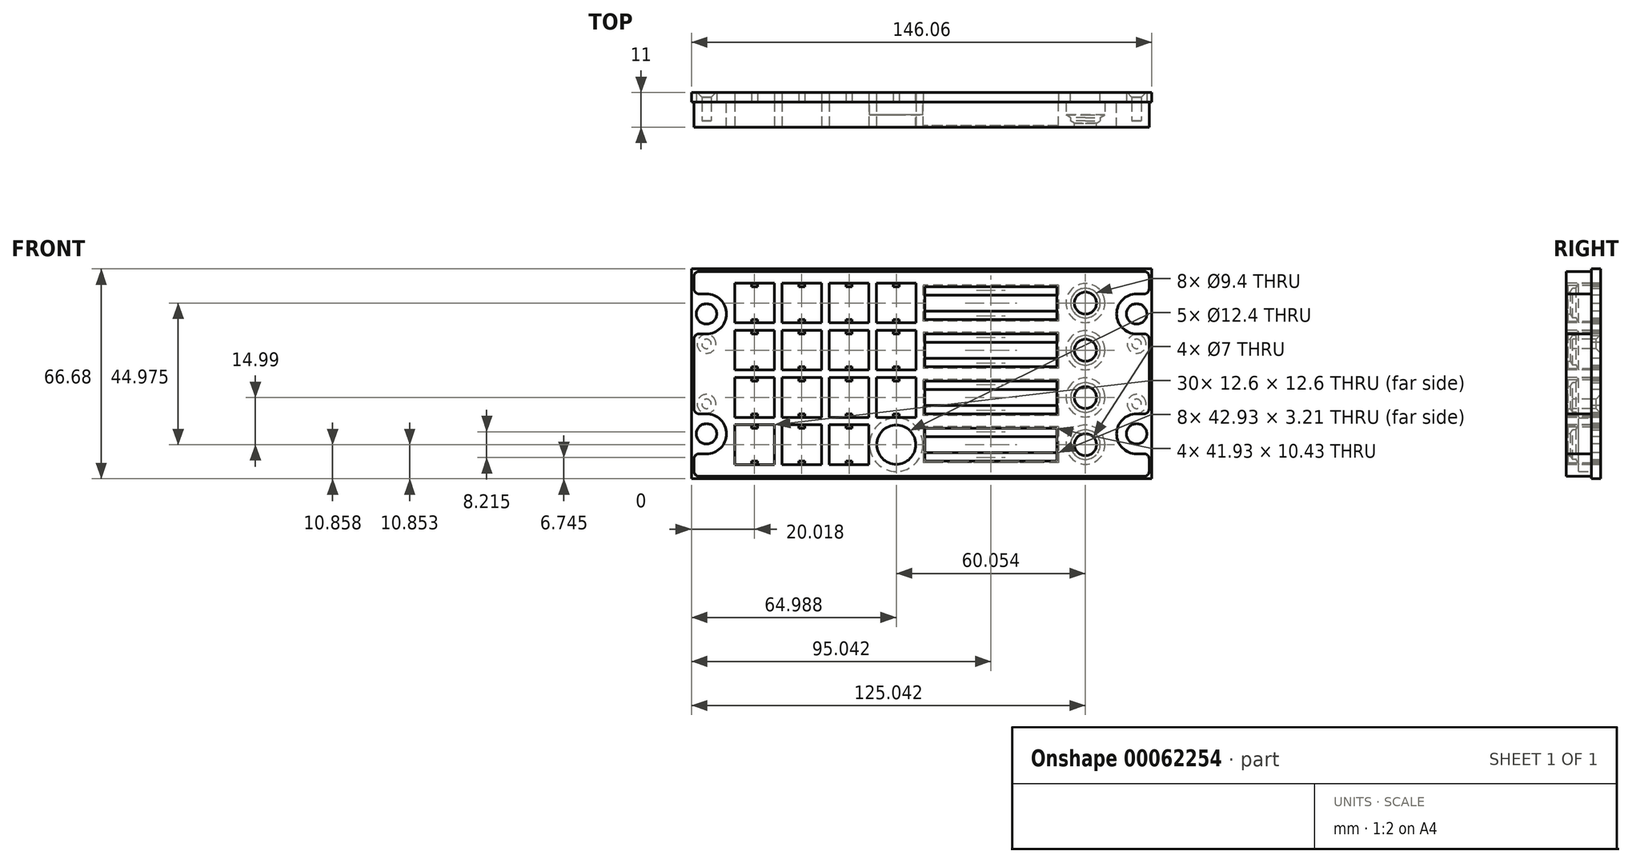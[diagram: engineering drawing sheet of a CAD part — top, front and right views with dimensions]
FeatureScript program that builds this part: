
annotation { "Feature Type Name" : "Feature", "Feature Type Description" : "" }
export const myFeature = defineFeature(function(context is Context, id is Id, definition is map)
    precondition{}
    {
        {
            var Q0;
            Q0=qCreatedBy(makeId("Front.planeOp"),FACE);
            var sketch = newSketch(context, id + "F0", { "sketchPlane" : qUnion([Q0])});
            skCircle(sketch, "E0", {"center": v(68.26, 19.05) * mm, "radius": 3.24 * mm});
            skCircle(sketch, "E1", {"center": v(68.26, -19.05) * mm, "radius": 3.24 * mm});
            skLineSegment(sketch, "E2", {"start": v(73.03, -33.34) * mm, "end": v(73.03, 33.34) * mm});
            skLineSegment(sketch, "E3", {"start": v(-73.03, 33.34) * mm, "end": v(73.03, 33.34) * mm});
            skLineSegment(sketch, "E4", {"start": v(-73.03, -33.34) * mm, "end": v(-73.03, 33.34) * mm});
            skLineSegment(sketch, "E5", {"start": v(73.03, -33.34) * mm, "end": v(-73.03, -33.34) * mm});
            skCircle(sketch, "E6", {"center": v(-68.26, -19.05) * mm, "radius": 3.24 * mm});
            skCircle(sketch, "E7", {"center": v(-68.26, 19.05) * mm, "radius": 3.24 * mm});
            skSolve(sketch);
        }
        {
            var Q0;
            Q0=makeQuery(id+"F0.imprint","IMPRINT",FACE,{"disambiguationData":[TD([[makeQuery(id+"F0.imprint","IMPRINT",EDGE,{"derivedFrom":sQuery(id+"F0.wireOp",EDGE,"E3")}),-1.0]])]});
            var Q1;
            Q1=makeQuery(id+"F0.imprint","IMPRINT",FACE,{"disambiguationData":[TD([[makeQuery(id+"F0.imprint","IMPRINT",EDGE,{"derivedFrom":sQuery(id+"F0.wireOp",EDGE,"PkqqOQiF-yNax-qwMA-xXQ1-8JkGYJM5UorW")}),-1.0]])]});
            var Q2;
            Q2=makeQuery(id+"F0.imprint","IMPRINT",FACE,{"disambiguationData":[TD([[makeQuery(id+"F0.imprint","IMPRINT",EDGE,{"derivedFrom":sQuery(id+"F0.wireOp",EDGE,"mQLwxlvx-ERE5-Mz6w-w5xm-fzkBPykc801v")}),-1.0]])]});
            var Q3;
            {var subQ0=sQuery(id+"F0.wireOp",EDGE,"rYfaxixD-Fold-LEk9-B7Sj-y0uFZKrMDMnr");Q3=makeQuery(id+"F0.imprint","IMPRINT",FACE,{"disambiguationData":[TD([[makeQuery(id+"F0.imprint","IMPRINT",EDGE,{"derivedFrom":subQ0}),1.0]])]});}
            var Q4;
            {var subQ0=sQuery(id+"F0.wireOp",EDGE,"rYfaxixD-Fold-LEk9-B7Sj-y0uFZKrMDMnr");Q4=makeQuery(id+"F0.imprint","IMPRINT",FACE,{"disambiguationData":[TD([[makeQuery(id+"F0.imprint","IMPRINT",EDGE,{"derivedFrom":subQ0}),-1.0]])]});}
            var Q5;
            {var subQ0=sQuery(id+"F0.wireOp",EDGE,"O9xndx6B-X1w8-GipV-mM2N-SATMcNrLLSkd");Q5=makeQuery(id+"F0.imprint","IMPRINT",FACE,{"disambiguationData":[TD([[makeQuery(id+"F0.imprint","IMPRINT",EDGE,{"derivedFrom":subQ0}),1.0]])]});}
            var Q6;
            {var subQ0=sQuery(id+"F0.wireOp",EDGE,"O9xndx6B-X1w8-GipV-mM2N-SATMcNrLLSkd");Q6=makeQuery(id+"F0.imprint","IMPRINT",FACE,{"disambiguationData":[TD([[makeQuery(id+"F0.imprint","IMPRINT",EDGE,{"derivedFrom":subQ0}),-1.0]])]});}
            extrude(context, id + "F1", {"entities" : qUnion([Q0, Q1, Q2, Q3, Q4, Q5, Q6]), "oppositeDirection" : true, "depth" : 3 * mm});
        }
        {
            var Q0;
            Q0=makeQuery(id+"F0.imprint","IMPRINT",FACE,{"disambiguationData":[TD([[makeQuery(id+"F0.imprint","IMPRINT",EDGE,{"derivedFrom":sQuery(id+"F0.wireOp",EDGE,"E3")}),-1.0]])]});
            var sketch = newSketch(context, id + "F2", { "sketchPlane" : qUnion([Q0])});
            skLineSegment(sketch, "E8", {"start": v(-68.26, 12.7) * mm, "end": v(-72.23, 12.7) * mm});
            skArc(sketch, "E9", {"start": v(-68.26, -25.4) * mm, "mid": v(-61.91, -19.05) * mm, "end": v(-68.26, -12.7) * mm});
            skArc(sketch, "E10", {"start": v(68.26, -12.7) * mm, "mid": v(61.91, -19.05) * mm, "end": v(68.26, -25.4) * mm});
            skLineSegment(sketch, "E11", {"start": v(72.22, -32.54) * mm, "end": v(72.22, -25.4) * mm});
            skLineSegment(sketch, "E12", {"start": v(-72.23, -32.54) * mm, "end": v(-72.23, -25.4) * mm});
            skLineSegment(sketch, "E13", {"start": v(72.22, -32.54) * mm, "end": v(-72.23, -32.54) * mm});
            skArc(sketch, "E14", {"start": v(68.26, 25.4) * mm, "mid": v(61.91, 19.05) * mm, "end": v(68.26, 12.7) * mm});
            skLineSegment(sketch, "E15", {"start": v(-72.23, 32.54) * mm, "end": v(72.23, 32.54) * mm});
            skLineSegment(sketch, "E16", {"start": v(68.26, 12.7) * mm, "end": v(72.22, 12.7) * mm});
            skLineSegment(sketch, "E17", {"start": v(68.26, 25.4) * mm, "end": v(72.22, 25.4) * mm});
            skLineSegment(sketch, "E18", {"start": v(72.22, -12.7) * mm, "end": v(72.22, 12.7) * mm});
            skLineSegment(sketch, "E19", {"start": v(68.26, -12.7) * mm, "end": v(72.22, -12.7) * mm});
            skLineSegment(sketch, "E20", {"start": v(-68.26, -12.7) * mm, "end": v(-72.23, -12.7) * mm});
            skLineSegment(sketch, "E21", {"start": v(68.26, -25.4) * mm, "end": v(72.22, -25.4) * mm});
            skLineSegment(sketch, "E22", {"start": v(-72.23, -12.7) * mm, "end": v(-72.23, 12.7) * mm});
            skArc(sketch, "E23", {"start": v(-68.26, 12.7) * mm, "mid": v(-61.91, 19.05) * mm, "end": v(-68.26, 25.4) * mm});
            skLineSegment(sketch, "E24", {"start": v(-72.23, 25.4) * mm, "end": v(-72.23, 32.54) * mm});
            skLineSegment(sketch, "E25", {"start": v(-68.26, 25.4) * mm, "end": v(-72.23, 25.4) * mm});
            skLineSegment(sketch, "E26", {"start": v(-68.26, -25.4) * mm, "end": v(-72.23, -25.4) * mm});
            skLineSegment(sketch, "E27", {"start": v(72.22, 25.4) * mm, "end": v(72.22, 32.54) * mm});
            skCircle(sketch, "E28", {"center": v(68.26, 19.05) * mm, "radius": 3.24 * mm});
            skCircle(sketch, "E29", {"center": v(68.26, -19.05) * mm, "radius": 3.24 * mm});
            skLineSegment(sketch, "E30", {"start": v(73.03, -33.34) * mm, "end": v(73.03, 33.34) * mm});
            skLineSegment(sketch, "E31", {"start": v(-73.03, 33.34) * mm, "end": v(73.03, 33.34) * mm});
            skLineSegment(sketch, "E32", {"start": v(-73.03, -33.34) * mm, "end": v(-73.03, 33.34) * mm});
            skLineSegment(sketch, "E33", {"start": v(73.03, -33.34) * mm, "end": v(-73.03, -33.34) * mm});
            skCircle(sketch, "E34", {"center": v(-68.26, -19.05) * mm, "radius": 3.24 * mm});
            skCircle(sketch, "E35", {"center": v(-68.26, 19.05) * mm, "radius": 3.24 * mm});
            skPoint(sketch, "E36.middle", {"position": v(-53.01, 22.49) * mm});
            skPoint(sketch, "E37.middle", {"position": v(-53.01, 7.5) * mm});
            skLineSegment(sketch, "E38", {"start": v(-53.01, 22.49) * mm, "end": v(-53.01, 23.47) * mm});
            skLineSegment(sketch, "E39", {"start": v(-53.01, 22.49) * mm, "end": v(-52.23, 22.49) * mm});
            skLineSegment(sketch, "E40.MirrorCS", {"start": v(-50.56, 16.89) * mm, "end": v(-50.56, 16.29) * mm});
            skLineSegment(sketch, "E41", {"start": v(-51.55, 16.29) * mm, "end": v(-51.55, 13.7) * mm});
            skLineSegment(sketch, "E42", {"start": v(-45.52, 24.36) * mm, "end": v(-45.52, 21.49) * mm});
            skLineSegment(sketch, "E43", {"start": v(-51.55, 15) * mm, "end": v(-52.76, 15) * mm});
            skPoint(sketch, "E44", {"position": v(-45.52, 22.92) * mm});
            skPoint(sketch, "E45", {"position": v(-52.76, 15) * mm});
            skPoint(sketch, "E46", {"position": v(-30.53, 22.49) * mm});
            skLineSegment(sketch, "E47.bottom", {"start": v(-46.76, 13.75) * mm, "end": v(-59.26, 13.75) * mm});
            skLineSegment(sketch, "E47.top", {"start": v(-46.76, 1.25) * mm, "end": v(-59.26, 1.25) * mm});
            skLineSegment(sketch, "E47.left", {"start": v(-46.76, 13.75) * mm, "end": v(-46.76, 1.25) * mm});
            skLineSegment(sketch, "E47.right", {"start": v(-59.26, 13.75) * mm, "end": v(-59.26, 1.25) * mm});
            skLineSegment(sketch, "E48.MirrorCS", {"start": v(-46.76, 16.24) * mm, "end": v(-59.26, 16.24) * mm});
            skLineSegment(sketch, "E49.MirrorCS", {"start": v(-59.26, 16.24) * mm, "end": v(-59.26, 28.74) * mm});
            skLineSegment(sketch, "E50.MirrorCS", {"start": v(-46.76, 16.24) * mm, "end": v(-46.76, 28.74) * mm});
            skLineSegment(sketch, "E51.MirrorCS", {"start": v(-46.76, 28.74) * mm, "end": v(-59.26, 28.74) * mm});
            skLineSegment(sketch, "E52.MirrorCS", {"start": v(-44.27, 16.24) * mm, "end": v(-44.27, 28.74) * mm});
            skLineSegment(sketch, "E53.MirrorCS", {"start": v(-44.27, 28.74) * mm, "end": v(-31.77, 28.74) * mm});
            skLineSegment(sketch, "E54.MirrorCS", {"start": v(-31.77, 16.24) * mm, "end": v(-31.77, 28.74) * mm});
            skLineSegment(sketch, "E55.MirrorCS", {"start": v(-44.27, 16.24) * mm, "end": v(-31.77, 16.24) * mm});
            skLineSegment(sketch, "E56", {"start": v(-30.53, 22.49) * mm, "end": v(-30.53, 24.6) * mm});
            skLineSegment(sketch, "E57.MirrorCS", {"start": v(-29.28, 16.24) * mm, "end": v(-29.28, 28.74) * mm});
            skLineSegment(sketch, "E58.MirrorCS", {"start": v(-16.78, 28.74) * mm, "end": v(-29.28, 28.74) * mm});
            skLineSegment(sketch, "E59.MirrorCS", {"start": v(-14.3, 28.74) * mm, "end": v(-1.8, 28.74) * mm});
            skLineSegment(sketch, "E60.MirrorCS", {"start": v(-1.8, 16.24) * mm, "end": v(-1.8, 28.74) * mm});
            skLineSegment(sketch, "E61.MirrorCS", {"start": v(-14.3, 16.24) * mm, "end": v(-1.8, 16.24) * mm});
            skLineSegment(sketch, "E62.MirrorCS", {"start": v(-14.3, 16.24) * mm, "end": v(-14.3, 28.74) * mm});
            skLineSegment(sketch, "E63.MirrorCS", {"start": v(-16.78, 16.24) * mm, "end": v(-16.78, 28.74) * mm});
            skLineSegment(sketch, "E64.MirrorCS", {"start": v(-16.78, 16.24) * mm, "end": v(-29.28, 16.24) * mm});
            skLineSegment(sketch, "E65.MirrorCS", {"start": v(-29.28, 13.75) * mm, "end": v(-29.28, 1.25) * mm});
            skLineSegment(sketch, "E66.MirrorCS", {"start": v(-30.53, 7.5) * mm, "end": v(-30.53, 5.4) * mm});
            skLineSegment(sketch, "E67.MirrorCS", {"start": v(-44.27, 13.75) * mm, "end": v(-31.77, 13.75) * mm});
            skLineSegment(sketch, "E68.MirrorCS", {"start": v(-16.78, 1.25) * mm, "end": v(-29.28, 1.25) * mm});
            skPoint(sketch, "E69.MirrorP", {"position": v(-30.53, 7.5) * mm});
            skLineSegment(sketch, "E70.MirrorCS", {"start": v(-16.78, 13.75) * mm, "end": v(-16.78, 1.25) * mm});
            skLineSegment(sketch, "E71.MirrorCS", {"start": v(-14.3, 1.25) * mm, "end": v(-1.8, 1.25) * mm});
            skLineSegment(sketch, "E72.MirrorCS", {"start": v(-44.27, 13.75) * mm, "end": v(-44.27, 1.25) * mm});
            skLineSegment(sketch, "E73.MirrorCS", {"start": v(-14.3, 13.75) * mm, "end": v(-1.8, 13.75) * mm});
            skLineSegment(sketch, "E74.MirrorCS", {"start": v(-14.3, 13.75) * mm, "end": v(-14.3, 1.25) * mm});
            skLineSegment(sketch, "E75.MirrorCS", {"start": v(-44.27, 1.25) * mm, "end": v(-31.77, 1.25) * mm});
            skLineSegment(sketch, "E76.MirrorCS", {"start": v(-31.77, 13.75) * mm, "end": v(-31.77, 1.25) * mm});
            skLineSegment(sketch, "E77.MirrorCS", {"start": v(-1.8, 13.75) * mm, "end": v(-1.8, 1.25) * mm});
            skPoint(sketch, "E78.MirrorP", {"position": v(-45.52, 7.06) * mm});
            skLineSegment(sketch, "E79.MirrorCS", {"start": v(-16.78, 13.75) * mm, "end": v(-29.28, 13.75) * mm});
            skLineSegment(sketch, "E80.MirrorCS", {"start": v(-53.01, -22.49) * mm, "end": v(-52.23, -22.49) * mm});
            skLineSegment(sketch, "E81.MirrorCS", {"start": v(-53.01, -22.49) * mm, "end": v(-53.01, -23.47) * mm});
            skPoint(sketch, "E82.MirrorP", {"position": v(-53.01, -7.5) * mm});
            skLineSegment(sketch, "E83.MirrorCS", {"start": v(-29.28, -13.75) * mm, "end": v(-29.28, -1.25) * mm});
            skLineSegment(sketch, "E84.MirrorCS", {"start": v(-30.53, -7.5) * mm, "end": v(-30.53, -5.4) * mm});
            skLineSegment(sketch, "E85.MirrorCS", {"start": v(-51.55, -15) * mm, "end": v(-52.76, -15) * mm});
            skLineSegment(sketch, "E86.MirrorCS", {"start": v(-51.55, -16.29) * mm, "end": v(-51.55, -13.7) * mm});
            skLineSegment(sketch, "E87.MirrorCS", {"start": v(-29.28, -16.24) * mm, "end": v(-29.28, -28.74) * mm});
            skLineSegment(sketch, "E88.MirrorCS", {"start": v(-50.56, -16.89) * mm, "end": v(-50.56, -16.29) * mm});
            skLineSegment(sketch, "E89.MirrorCS", {"start": v(-30.53, -22.49) * mm, "end": v(-30.53, -24.6) * mm});
            skLineSegment(sketch, "E90.MirrorCS", {"start": v(-45.52, -24.36) * mm, "end": v(-45.52, -21.49) * mm});
            skPoint(sketch, "E91.MirrorP", {"position": v(-53.01, -22.49) * mm});
            skLineSegment(sketch, "E92.MirrorCS", {"start": v(-46.76, -1.25) * mm, "end": v(-59.26, -1.25) * mm});
            skPoint(sketch, "E93.MirrorP", {"position": v(-52.76, -15) * mm});
            skPoint(sketch, "E94.MirrorP", {"position": v(-45.52, -7.06) * mm});
            skPoint(sketch, "E95.MirrorP", {"position": v(-45.52, -22.92) * mm});
            skLineSegment(sketch, "E96.MirrorCS", {"start": v(-31.77, -16.24) * mm, "end": v(-31.77, -28.74) * mm});
            skLineSegment(sketch, "E97.MirrorCS", {"start": v(-44.27, -28.74) * mm, "end": v(-31.77, -28.74) * mm});
            skLineSegment(sketch, "E98.MirrorCS", {"start": v(-44.27, -1.25) * mm, "end": v(-31.77, -1.25) * mm});
            skLineSegment(sketch, "E99.MirrorCS", {"start": v(-16.78, -1.25) * mm, "end": v(-29.28, -1.25) * mm});
            skLineSegment(sketch, "E100.MirrorCS", {"start": v(-16.78, -13.75) * mm, "end": v(-16.78, -1.25) * mm});
            skLineSegment(sketch, "E101.MirrorCS", {"start": v(-31.77, -13.75) * mm, "end": v(-31.77, -1.25) * mm});
            skLineSegment(sketch, "E102.MirrorCS", {"start": v(-14.3, -13.75) * mm, "end": v(-1.8, -13.75) * mm});
            skLineSegment(sketch, "E103.MirrorCS", {"start": v(-59.26, -13.75) * mm, "end": v(-59.26, -1.25) * mm});
            skLineSegment(sketch, "E104.MirrorCS", {"start": v(-14.3, -13.75) * mm, "end": v(-14.3, -1.25) * mm});
            skLineSegment(sketch, "E105.MirrorCS", {"start": v(-44.27, -16.24) * mm, "end": v(-44.27, -28.74) * mm});
            skLineSegment(sketch, "E106.MirrorCS", {"start": v(-16.78, -28.74) * mm, "end": v(-29.28, -28.74) * mm});
            skLineSegment(sketch, "E107.MirrorCS", {"start": v(-16.78, -16.24) * mm, "end": v(-29.28, -16.24) * mm});
            skLineSegment(sketch, "E108.MirrorCS", {"start": v(-1.8, -13.75) * mm, "end": v(-1.8, -1.25) * mm});
            skLineSegment(sketch, "E109.MirrorCS", {"start": v(-44.27, -16.24) * mm, "end": v(-31.77, -16.24) * mm});
            skLineSegment(sketch, "E110.MirrorCS", {"start": v(-14.3, -1.25) * mm, "end": v(-1.8, -1.25) * mm});
            skLineSegment(sketch, "E111.MirrorCS", {"start": v(-46.76, -16.24) * mm, "end": v(-59.26, -16.24) * mm});
            skLineSegment(sketch, "E112.MirrorCS", {"start": v(-46.76, -16.24) * mm, "end": v(-46.76, -28.74) * mm});
            skLineSegment(sketch, "E113.MirrorCS", {"start": v(-59.26, -16.24) * mm, "end": v(-59.26, -28.74) * mm});
            skLineSegment(sketch, "E114.MirrorCS", {"start": v(-16.78, -16.24) * mm, "end": v(-16.78, -28.74) * mm});
            skLineSegment(sketch, "E115.MirrorCS", {"start": v(-46.76, -13.75) * mm, "end": v(-46.76, -1.25) * mm});
            skLineSegment(sketch, "E116.MirrorCS", {"start": v(-44.27, -13.75) * mm, "end": v(-31.77, -13.75) * mm});
            skLineSegment(sketch, "E117.MirrorCS", {"start": v(-16.78, -13.75) * mm, "end": v(-29.28, -13.75) * mm});
            skLineSegment(sketch, "E118.MirrorCS", {"start": v(-46.76, -28.74) * mm, "end": v(-59.26, -28.74) * mm});
            skPoint(sketch, "E119.MirrorP", {"position": v(-30.53, -22.49) * mm});
            skPoint(sketch, "E120.MirrorP", {"position": v(-30.53, -7.5) * mm});
            skLineSegment(sketch, "E121.MirrorCS", {"start": v(-44.27, -13.75) * mm, "end": v(-44.27, -1.25) * mm});
            skLineSegment(sketch, "E122.MirrorCS", {"start": v(-46.76, -13.75) * mm, "end": v(-59.26, -13.75) * mm});
            skLineSegment(sketch, "E123.bottom", {"start": v(-59.26, 28.74) * mm, "end": v(-58.01, 28.74) * mm});
            skLineSegment(sketch, "E123.top", {"start": v(-59.26, 27.49) * mm, "end": v(-58.01, 27.49) * mm});
            skLineSegment(sketch, "E123.left", {"start": v(-59.26, 28.74) * mm, "end": v(-59.26, 27.49) * mm});
            skLineSegment(sketch, "E123.right", {"start": v(-58.01, 28.74) * mm, "end": v(-58.01, 27.49) * mm});
            skLineSegment(sketch, "E124.MirrorCS", {"start": v(-48.01, 28.74) * mm, "end": v(-48.01, 27.49) * mm});
            skLineSegment(sketch, "E125.MirrorCS", {"start": v(-46.76, 27.49) * mm, "end": v(-48.01, 27.49) * mm});
            skLineSegment(sketch, "E126.MirrorCS", {"start": v(-43.02, 28.74) * mm, "end": v(-43.02, 27.49) * mm});
            skLineSegment(sketch, "E127.MirrorCS", {"start": v(-44.27, 27.49) * mm, "end": v(-43.02, 27.49) * mm});
            skLineSegment(sketch, "E128.MirrorCS", {"start": v(-33.02, 28.74) * mm, "end": v(-33.02, 27.49) * mm});
            skLineSegment(sketch, "E129.MirrorCS", {"start": v(-31.77, 27.49) * mm, "end": v(-33.02, 27.49) * mm});
            skLineSegment(sketch, "E130.MirrorCS", {"start": v(-28.03, 28.74) * mm, "end": v(-28.03, 27.49) * mm});
            skLineSegment(sketch, "E131.MirrorCS", {"start": v(-29.28, 27.49) * mm, "end": v(-28.03, 27.49) * mm});
            skLineSegment(sketch, "E132.MirrorCS", {"start": v(-18.03, 28.74) * mm, "end": v(-18.03, 27.49) * mm});
            skLineSegment(sketch, "E133.MirrorCS", {"start": v(-16.78, 27.49) * mm, "end": v(-18.03, 27.49) * mm});
            skLineSegment(sketch, "E134.MirrorCS", {"start": v(-13.04, 28.74) * mm, "end": v(-13.04, 27.49) * mm});
            skLineSegment(sketch, "E135.MirrorCS", {"start": v(-14.3, 27.49) * mm, "end": v(-13.04, 27.49) * mm});
            skLineSegment(sketch, "E136.MirrorCS", {"start": v(-3.04, 28.74) * mm, "end": v(-3.04, 27.49) * mm});
            skLineSegment(sketch, "E137.MirrorCS", {"start": v(-1.8, 27.49) * mm, "end": v(-3.04, 27.49) * mm});
            skLineSegment(sketch, "E138.bottom", {"start": v(-59.26, 13.75) * mm, "end": v(-58.01, 13.75) * mm});
            skLineSegment(sketch, "E138.top", {"start": v(-59.26, 12.5) * mm, "end": v(-58.01, 12.5) * mm});
            skLineSegment(sketch, "E138.left", {"start": v(-59.26, 13.75) * mm, "end": v(-59.26, 12.5) * mm});
            skLineSegment(sketch, "E138.right", {"start": v(-58.01, 13.75) * mm, "end": v(-58.01, 12.5) * mm});
            skLineSegment(sketch, "E139.MirrorCS", {"start": v(-48.01, 13.75) * mm, "end": v(-48.01, 12.5) * mm});
            skLineSegment(sketch, "E140.MirrorCS", {"start": v(-46.76, 12.5) * mm, "end": v(-48.01, 12.5) * mm});
            skLineSegment(sketch, "E141.MirrorCS", {"start": v(-33.02, 13.75) * mm, "end": v(-33.02, 12.5) * mm});
            skLineSegment(sketch, "E142.MirrorCS", {"start": v(-31.77, 12.5) * mm, "end": v(-33.02, 12.5) * mm});
            skLineSegment(sketch, "E143.MirrorCS", {"start": v(-43.02, 13.75) * mm, "end": v(-43.02, 12.5) * mm});
            skLineSegment(sketch, "E144.MirrorCS", {"start": v(-44.27, 12.5) * mm, "end": v(-43.02, 12.5) * mm});
            skLineSegment(sketch, "E145.MirrorCS", {"start": v(-28.03, 13.75) * mm, "end": v(-28.03, 12.5) * mm});
            skLineSegment(sketch, "E146.MirrorCS", {"start": v(-29.28, 12.5) * mm, "end": v(-28.03, 12.5) * mm});
            skLineSegment(sketch, "E147.MirrorCS", {"start": v(-18.03, 13.75) * mm, "end": v(-18.03, 12.5) * mm});
            skLineSegment(sketch, "E148.MirrorCS", {"start": v(-16.78, 12.5) * mm, "end": v(-18.03, 12.5) * mm});
            skLineSegment(sketch, "E149.MirrorCS", {"start": v(-3.04, 13.75) * mm, "end": v(-3.04, 12.5) * mm});
            skLineSegment(sketch, "E150.MirrorCS", {"start": v(-1.8, 12.5) * mm, "end": v(-3.04, 12.5) * mm});
            skLineSegment(sketch, "E151.MirrorCS", {"start": v(-13.04, 13.75) * mm, "end": v(-13.04, 12.5) * mm});
            skLineSegment(sketch, "E152.MirrorCS", {"start": v(-14.3, 12.5) * mm, "end": v(-13.04, 12.5) * mm});
            skLineSegment(sketch, "E153.bottom", {"start": v(-59.26, -1.25) * mm, "end": v(-58.01, -1.25) * mm});
            skLineSegment(sketch, "E153.top", {"start": v(-59.26, -2.5) * mm, "end": v(-58.01, -2.5) * mm});
            skLineSegment(sketch, "E153.left", {"start": v(-59.26, -1.25) * mm, "end": v(-59.26, -2.5) * mm});
            skLineSegment(sketch, "E153.right", {"start": v(-58.01, -1.25) * mm, "end": v(-58.01, -2.5) * mm});
            skLineSegment(sketch, "E154.MirrorCS", {"start": v(-48.01, -1.25) * mm, "end": v(-48.01, -2.5) * mm});
            skLineSegment(sketch, "E155.MirrorCS", {"start": v(-46.76, -2.5) * mm, "end": v(-48.01, -2.5) * mm});
            skLineSegment(sketch, "E156.MirrorCS", {"start": v(-43.02, -1.25) * mm, "end": v(-43.02, -2.5) * mm});
            skLineSegment(sketch, "E157.MirrorCS", {"start": v(-44.27, -2.5) * mm, "end": v(-43.02, -2.5) * mm});
            skLineSegment(sketch, "E158.MirrorCS", {"start": v(-33.02, -1.25) * mm, "end": v(-33.02, -2.5) * mm});
            skLineSegment(sketch, "E159.MirrorCS", {"start": v(-31.77, -2.5) * mm, "end": v(-33.02, -2.5) * mm});
            skLineSegment(sketch, "E160.MirrorCS", {"start": v(-60.5, -7.5) * mm, "end": v(-60.5, -5.4) * mm});
            skLineSegment(sketch, "E161.MirrorCS", {"start": v(-1.8, -2.5) * mm, "end": v(-3.04, -2.5) * mm});
            skLineSegment(sketch, "E162.MirrorCS", {"start": v(-3.04, -1.25) * mm, "end": v(-3.04, -2.5) * mm});
            skLineSegment(sketch, "E163.MirrorCS", {"start": v(-13.04, -1.25) * mm, "end": v(-13.04, -2.5) * mm});
            skLineSegment(sketch, "E164.MirrorCS", {"start": v(-14.3, -2.5) * mm, "end": v(-13.04, -2.5) * mm});
            skLineSegment(sketch, "E165.MirrorCS", {"start": v(-16.78, -2.5) * mm, "end": v(-18.03, -2.5) * mm});
            skLineSegment(sketch, "E166.MirrorCS", {"start": v(-18.03, -1.25) * mm, "end": v(-18.03, -2.5) * mm});
            skLineSegment(sketch, "E167.MirrorCS", {"start": v(-28.03, -1.25) * mm, "end": v(-28.03, -2.5) * mm});
            skLineSegment(sketch, "E168.MirrorCS", {"start": v(-29.28, -2.5) * mm, "end": v(-28.03, -2.5) * mm});
            skLineSegment(sketch, "E169.bottom", {"start": v(-59.26, -16.24) * mm, "end": v(-58.01, -16.24) * mm});
            skLineSegment(sketch, "E169.top", {"start": v(-59.26, -17.49) * mm, "end": v(-58.01, -17.49) * mm});
            skLineSegment(sketch, "E169.left", {"start": v(-59.26, -16.24) * mm, "end": v(-59.26, -17.49) * mm});
            skLineSegment(sketch, "E169.right", {"start": v(-58.01, -16.24) * mm, "end": v(-58.01, -17.49) * mm});
            skLineSegment(sketch, "E170.MirrorCS", {"start": v(-48.01, -16.24) * mm, "end": v(-48.01, -17.49) * mm});
            skLineSegment(sketch, "E171.MirrorCS", {"start": v(-46.76, -17.49) * mm, "end": v(-48.01, -17.49) * mm});
            skLineSegment(sketch, "E172.MirrorCS", {"start": v(-43.02, -16.24) * mm, "end": v(-43.02, -17.49) * mm});
            skLineSegment(sketch, "E173.MirrorCS", {"start": v(-44.27, -17.49) * mm, "end": v(-43.02, -17.49) * mm});
            skLineSegment(sketch, "E174.MirrorCS", {"start": v(-33.02, -16.24) * mm, "end": v(-33.02, -17.49) * mm});
            skLineSegment(sketch, "E175.MirrorCS", {"start": v(-31.77, -17.49) * mm, "end": v(-33.02, -17.49) * mm});
            skLineSegment(sketch, "E176.MirrorCS", {"start": v(-28.03, -16.24) * mm, "end": v(-28.03, -17.49) * mm});
            skLineSegment(sketch, "E177.MirrorCS", {"start": v(-29.28, -17.49) * mm, "end": v(-28.03, -17.49) * mm});
            skLineSegment(sketch, "E178.MirrorCS", {"start": v(-18.03, -16.24) * mm, "end": v(-18.03, -17.49) * mm});
            skLineSegment(sketch, "E179.MirrorCS", {"start": v(-16.78, -17.49) * mm, "end": v(-18.03, -17.49) * mm});
            skSolve(sketch);
        }
        {
            var Q0;
            Q0=makeQuery(id+"F2.imprint","IMPRINT",FACE,{"disambiguationData":[TD([[makeQuery(id+"F2.imprint","IMPRINT",EDGE,{"derivedFrom":sQuery(id+"F2.wireOp",EDGE,"E25")}),-1.0]])]});
            var Q1;
            Q1=makeQuery(id+"F2.imprint","IMPRINT",FACE,{"disambiguationData":[TD([[makeQuery(id+"F2.imprint","IMPRINT",EDGE,{"derivedFrom":sQuery(id+"F2.wireOp",EDGE,"E19")}),1.0]])]});
            var Q2;
            Q2=makeQuery(id+"F2.imprint","IMPRINT",FACE,{"disambiguationData":[TD([[makeQuery(id+"F2.imprint","IMPRINT",EDGE,{"derivedFrom":sQuery(id+"F2.wireOp",EDGE,"qFL4g8N9-Z4pU-GTXp-8CAc-8JK48FUQn30E")}),-1.0]])]});
            var Q3;
            {var subQ0=sQuery(id+"F2.wireOp",EDGE,"8300f3b8-7403-4ca9-be41-47c3c9048a200.MirrorCS");var subQ1=sQuery(id+"F2.wireOp",EDGE,"vQyVyV5x-p2yk-mqKs-SuCr-8gVJOWqc7IX1");var subQ2=makeQuery(id+"F2.imprint","INTERSECT",VERTEX,{"disambiguationData":[OD(0.0)],"derivedFrom":[subQ1,subQ0]});Q3=makeQuery(id+"F2.imprint","IMPRINT",FACE,{"disambiguationData":[TD([[makeQuery(id+"F2.imprint","IMPRINT",EDGE,{"disambiguationData":[TD([[subQ2,-1.0]])],"derivedFrom":subQ1}),-1.0]])]});}
            var Q4;
            {var subQ0=sQuery(id+"F2.wireOp",EDGE,"2a6b824b-4dab-4004-b1fb-ce6e91d1ccc60.MirrorCS");var subQ1=sQuery(id+"F2.wireOp",EDGE,"vQyVyV5x-p2yk-mqKs-SuCr-8gVJOWqc7IX1");var subQ2=makeQuery(id+"F2.imprint","INTERSECT",VERTEX,{"disambiguationData":[OD(1.0)],"derivedFrom":[subQ1,subQ0]});Q4=makeQuery(id+"F2.imprint","IMPRINT",FACE,{"disambiguationData":[TD([[makeQuery(id+"F2.imprint","IMPRINT",EDGE,{"disambiguationData":[TD([[subQ2,-1.0]])],"derivedFrom":subQ1}),-1.0]])]});}
            var Q5;
            {var subQ1=sQuery(id+"F2.wireOp",EDGE,"670ac697-91f2-46ae-bd51-22720ef3b4b70.MirrorCS");var subQ7=sQuery(id+"F2.wireOp",EDGE,"vQyVyV5x-p2yk-mqKs-SuCr-8gVJOWqc7IX1");var subQ9=makeQuery(id+"F2.imprint","INTERSECT",VERTEX,{"disambiguationData":[OD(0.0)],"derivedFrom":[subQ7,subQ1]});Q5=makeQuery(id+"F2.imprint","IMPRINT",FACE,{"disambiguationData":[TD([[makeQuery(id+"F2.imprint","IMPRINT",EDGE,{"disambiguationData":[TD([[subQ9,-1.0]])],"derivedFrom":subQ7}),-1.0]])]});}
            var Q6;
            {var subQ1=sQuery(id+"F2.wireOp",EDGE,"b885f9d6-6f88-434f-8d35-7eda18fda9920.MirrorCS");var subQ10=sQuery(id+"F2.wireOp",EDGE,"fd58afc0-6d7a-4a91-a401-fc694c61853e0.MirrorCS");var subQ11=makeQuery(id+"F2.imprint","INTERSECT",VERTEX,{"derivedFrom":[subQ10,subQ1]});Q6=makeQuery(id+"F2.imprint","IMPRINT",FACE,{"disambiguationData":[TD([[makeQuery(id+"F2.imprint","IMPRINT",EDGE,{"disambiguationData":[TD([[subQ11,-1.0]])],"derivedFrom":subQ10}),1.0]])]});}
            var Q7;
            {var subQ5=sQuery(id+"F2.wireOp",EDGE,"f7391f9a-cba1-4bdd-97ca-affd80be98fc0.MirrorCS");var subQ7=sQuery(id+"F2.wireOp",EDGE,"vQyVyV5x-p2yk-mqKs-SuCr-8gVJOWqc7IX1");var subQ9=makeQuery(id+"F2.imprint","INTERSECT",VERTEX,{"disambiguationData":[OD(1.0)],"derivedFrom":[subQ7,subQ5]});Q7=makeQuery(id+"F2.imprint","IMPRINT",FACE,{"disambiguationData":[TD([[makeQuery(id+"F2.imprint","IMPRINT",EDGE,{"disambiguationData":[TD([[subQ9,-1.0]])],"derivedFrom":subQ7}),-1.0]])]});}
            var Q8;
            {var subQ0=sQuery(id+"F2.wireOp",EDGE,"a0aa284d-f75d-465f-ae83-bcdf0bee77cb0.MirrorCS");var subQ1=sQuery(id+"F2.wireOp",EDGE,"vQyVyV5x-p2yk-mqKs-SuCr-8gVJOWqc7IX1");var subQ2=makeQuery(id+"F2.imprint","INTERSECT",VERTEX,{"disambiguationData":[OD(0.0)],"derivedFrom":[subQ1,subQ0]});Q8=makeQuery(id+"F2.imprint","IMPRINT",FACE,{"disambiguationData":[TD([[makeQuery(id+"F2.imprint","IMPRINT",EDGE,{"disambiguationData":[TD([[subQ2,-1.0]])],"derivedFrom":subQ1}),-1.0]])]});}
            var Q9;
            {var subQ0=sQuery(id+"F2.wireOp",EDGE,"a3543952-6d5b-4532-924e-545850e177ff0.MirrorCS");var subQ1=sQuery(id+"F2.wireOp",EDGE,"vQyVyV5x-p2yk-mqKs-SuCr-8gVJOWqc7IX1");var subQ2=makeQuery(id+"F2.imprint","INTERSECT",VERTEX,{"disambiguationData":[OD(0.0)],"derivedFrom":[subQ1,subQ0]});Q9=makeQuery(id+"F2.imprint","IMPRINT",FACE,{"disambiguationData":[TD([[makeQuery(id+"F2.imprint","IMPRINT",EDGE,{"disambiguationData":[TD([[subQ2,-1.0]])],"derivedFrom":subQ1}),-1.0]])]});}
            var Q10;
            {var subQ0=sQuery(id+"F2.wireOp",EDGE,"890764af-804e-4d47-b915-99d5968904e30.MirrorCS");var subQ1=sQuery(id+"F2.wireOp",EDGE,"vQyVyV5x-p2yk-mqKs-SuCr-8gVJOWqc7IX1");var subQ2=makeQuery(id+"F2.imprint","INTERSECT",VERTEX,{"disambiguationData":[OD(0.0)],"derivedFrom":[subQ1,subQ0]});Q10=makeQuery(id+"F2.imprint","IMPRINT",FACE,{"disambiguationData":[TD([[makeQuery(id+"F2.imprint","IMPRINT",EDGE,{"disambiguationData":[TD([[subQ2,-1.0]])],"derivedFrom":subQ1}),-1.0]])]});}
            var Q11;
            {var subQ0=sQuery(id+"F2.wireOp",EDGE,"670ac697-91f2-46ae-bd51-22720ef3b4b70.MirrorCS");var subQ1=sQuery(id+"F2.wireOp",EDGE,"vQyVyV5x-p2yk-mqKs-SuCr-8gVJOWqc7IX1");var subQ2=makeQuery(id+"F2.imprint","INTERSECT",VERTEX,{"disambiguationData":[OD(1.0)],"derivedFrom":[subQ1,subQ0]});Q11=makeQuery(id+"F2.imprint","IMPRINT",FACE,{"disambiguationData":[TD([[makeQuery(id+"F2.imprint","IMPRINT",EDGE,{"disambiguationData":[TD([[subQ2,-1.0]])],"derivedFrom":subQ1}),-1.0]])]});}
            var Q12;
            {var subQ1=sQuery(id+"F2.wireOp",EDGE,"vQyVyV5x-p2yk-mqKs-SuCr-8gVJOWqc7IX1");var subQ6=sQuery(id+"F2.wireOp",EDGE,"a0aa284d-f75d-465f-ae83-bcdf0bee77cb0.MirrorCS");var subQ8=makeQuery(id+"F2.imprint","INTERSECT",VERTEX,{"disambiguationData":[OD(1.0)],"derivedFrom":[subQ1,subQ6]});Q12=makeQuery(id+"F2.imprint","IMPRINT",FACE,{"disambiguationData":[TD([[makeQuery(id+"F2.imprint","IMPRINT",EDGE,{"disambiguationData":[TD([[subQ8,-1.0]])],"derivedFrom":subQ1}),-1.0]])]});}
            extrude(context, id + "F3", {"entities" : qUnion([Q0, Q1, Q2, Q3, Q4, Q5, Q6, Q7, Q8, Q9, Q10, Q11, Q12]), "depth" : 8 * mm});
        }
        {
            var Q0;
            Q0=makeQuery(id+"F3.opExtrude","SWEPT_EDGE",EDGE,{"disambiguationData":[OSD([sQuery(id+"F2.wireOp",EDGE,"E12"),sQuery(id+"F2.wireOp",EDGE,"E13")])]});
            var Q1;
            Q1=makeQuery(id+"F3.opExtrude","SWEPT_EDGE",EDGE,{"disambiguationData":[OSD([sQuery(id+"F2.wireOp",EDGE,"E12"),sQuery(id+"F2.wireOp",EDGE,"E26")])]});
            var Q2;
            Q2=makeQuery(id+"F3.opExtrude","SWEPT_EDGE",EDGE,{"disambiguationData":[OSD([sQuery(id+"F2.wireOp",EDGE,"E20"),sQuery(id+"F2.wireOp",EDGE,"E22")])]});
            var Q3;
            Q3=makeQuery(id+"F3.opExtrude","SWEPT_EDGE",EDGE,{"disambiguationData":[OSD([sQuery(id+"F2.wireOp",EDGE,"E8"),sQuery(id+"F2.wireOp",EDGE,"E22")])]});
            var Q4;
            Q4=makeQuery(id+"F3.opExtrude","SWEPT_EDGE",EDGE,{"disambiguationData":[OSD([sQuery(id+"F2.wireOp",EDGE,"E25"),sQuery(id+"F2.wireOp",EDGE,"E24")])]});
            var Q5;
            Q5=makeQuery(id+"F3.opExtrude","SWEPT_EDGE",EDGE,{"disambiguationData":[OSD([sQuery(id+"F2.wireOp",EDGE,"E24"),sQuery(id+"F2.wireOp",EDGE,"E15")])]});
            var Q6;
            Q6=makeQuery(id+"F3.opExtrude","SWEPT_EDGE",EDGE,{"disambiguationData":[OSD([sQuery(id+"F2.wireOp",EDGE,"E11"),sQuery(id+"F2.wireOp",EDGE,"E13")])]});
            var Q7;
            Q7=makeQuery(id+"F3.opExtrude","SWEPT_EDGE",EDGE,{"disambiguationData":[OSD([sQuery(id+"F2.wireOp",EDGE,"E11"),sQuery(id+"F2.wireOp",EDGE,"E21")])]});
            var Q8;
            Q8=makeQuery(id+"F3.opExtrude","SWEPT_EDGE",EDGE,{"disambiguationData":[OSD([sQuery(id+"F2.wireOp",EDGE,"E19"),sQuery(id+"F2.wireOp",EDGE,"E18")])]});
            var Q9;
            Q9=makeQuery(id+"F3.opExtrude","SWEPT_EDGE",EDGE,{"disambiguationData":[OSD([sQuery(id+"F2.wireOp",EDGE,"E16"),sQuery(id+"F2.wireOp",EDGE,"E18")])]});
            var Q10;
            Q10=makeQuery(id+"F3.opExtrude","SWEPT_EDGE",EDGE,{"disambiguationData":[OSD([sQuery(id+"F2.wireOp",EDGE,"E17"),sQuery(id+"F2.wireOp",EDGE,"E27")])]});
            var Q11;
            Q11=makeQuery(id+"F3.opExtrude","SWEPT_EDGE",EDGE,{"disambiguationData":[OSD([sQuery(id+"F2.wireOp",EDGE,"E15"),sQuery(id+"F2.wireOp",EDGE,"E27")])]});
            fillet(context, id + "F4", {"entities" : qUnion([Q0, Q1, Q2, Q3, Q4, Q5, Q6, Q7, Q8, Q9, Q10, Q11]), "radius" : 1.59 * mm, "tangentPropagation" : true, "allowEdgeOverflow" : false});
        }
        {
            var Q0;
            Q0=makeQuery(id+"F3.opExtrude","CAP_FACE",FACE,{"disambiguationData":[OSD([sQuery(id+"F2.wireOp",EDGE,"E19"),sQuery(id+"F2.wireOp",EDGE,"E25"),sQuery(id+"F2.wireOp",EDGE,"E12"),sQuery(id+"F2.wireOp",EDGE,"E10"),sQuery(id+"F2.wireOp",EDGE,"E24"),sQuery(id+"F2.wireOp",EDGE,"E17"),sQuery(id+"F2.wireOp",EDGE,"E15"),sQuery(id+"F2.wireOp",EDGE,"E16"),sQuery(id+"F2.wireOp",EDGE,"E11"),sQuery(id+"F2.wireOp",EDGE,"E18"),sQuery(id+"F2.wireOp",EDGE,"E13"),sQuery(id+"F2.wireOp",EDGE,"E26"),sQuery(id+"F2.wireOp",EDGE,"E9"),sQuery(id+"F2.wireOp",EDGE,"E27"),sQuery(id+"F2.wireOp",EDGE,"E21"),sQuery(id+"F2.wireOp",EDGE,"E14"),sQuery(id+"F2.wireOp",EDGE,"E20"),sQuery(id+"F2.wireOp",EDGE,"E23"),sQuery(id+"F2.wireOp",EDGE,"E8"),sQuery(id+"F2.wireOp",EDGE,"E22"),sQuery(id+"F2.wireOp",EDGE,"qFL4g8N9-Z4pU-GTXp-8CAc-8JK48FUQn30E"),sQuery(id+"F2.wireOp",EDGE,"CwOBQIGn-MMQe-Slb5-Sy8z-p2TvoJb7h1UY"),sQuery(id+"F2.wireOp",EDGE,"44x8lHQw-1wNe-uae2-3r2V-fi1hMbBCpbwF"),sQuery(id+"F2.wireOp",EDGE,"JyooYvdZ-CdAV-iNBH-ClTq-EUTpPKcEytES"),sQuery(id+"F2.wireOp",EDGE,"vQyVyV5x-p2yk-mqKs-SuCr-8gVJOWqc7IX1"),sQuery(id+"F2.wireOp",EDGE,"E36.bottom"),sQuery(id+"F2.wireOp",EDGE,"E36.top"),sQuery(id+"F2.wireOp",EDGE,"E36.left"),sQuery(id+"F2.wireOp",EDGE,"E36.right"),sQuery(id+"F2.wireOp",EDGE,"E37.bottom"),sQuery(id+"F2.wireOp",EDGE,"E37.top"),sQuery(id+"F2.wireOp",EDGE,"E37.left"),sQuery(id+"F2.wireOp",EDGE,"E37.right"),sQuery(id+"F2.wireOp",EDGE,"7f746da5-9ad2-4a81-9fc8-e2dc20fbcc640.MirrorCS"),sQuery(id+"F2.wireOp",EDGE,"9dd7ed31-53ff-4210-8604-d896296ed41c0.MirrorCS"),sQuery(id+"F2.wireOp",EDGE,"c067bd87-fd3e-466a-810f-f065c564f8ed0.MirrorCS"),sQuery(id+"F2.wireOp",EDGE,"fd285260-f370-4225-87cf-36dfdc371af00.MirrorCS"),sQuery(id+"F2.wireOp",EDGE,"b8700096-e2a7-4ac0-8a1f-91fa73afae940.MirrorCS"),sQuery(id+"F2.wireOp",EDGE,"9a9e7c1c-7c8d-4d33-8a77-0f84e462b1150.MirrorCS"),sQuery(id+"F2.wireOp",EDGE,"c7a65c5f-7e80-4536-bd35-bc8f91e8c68b0.MirrorCS"),sQuery(id+"F2.wireOp",EDGE,"c29b3d01-277a-4ec0-8e36-8a23026f26020.MirrorCS"),sQuery(id+"F2.wireOp",EDGE,"0b7ba8dc-1e88-4324-a412-ce5f49a3f93b69.MirrorCS"),sQuery(id+"F2.wireOp",EDGE,"0b7ba8dc-1e88-4324-a412-ce5f49a3f93b71.MirrorCS"),sQuery(id+"F2.wireOp",EDGE,"0b7ba8dc-1e88-4324-a412-ce5f49a3f93b76.MirrorCS"),sQuery(id+"F2.wireOp",EDGE,"0b7ba8dc-1e88-4324-a412-ce5f49a3f93b78.MirrorCS"),sQuery(id+"F2.wireOp",EDGE,"0b7ba8dc-1e88-4324-a412-ce5f49a3f93b81.MirrorCS"),sQuery(id+"F2.wireOp",EDGE,"0b7ba8dc-1e88-4324-a412-ce5f49a3f93b82.MirrorCS"),sQuery(id+"F2.wireOp",EDGE,"0b7ba8dc-1e88-4324-a412-ce5f49a3f93b84.MirrorCS"),sQuery(id+"F2.wireOp",EDGE,"0b7ba8dc-1e88-4324-a412-ce5f49a3f93b86.MirrorCS"),sQuery(id+"F2.wireOp",EDGE,"0b7ba8dc-1e88-4324-a412-ce5f49a3f93b89.MirrorCS"),sQuery(id+"F2.wireOp",EDGE,"0b7ba8dc-1e88-4324-a412-ce5f49a3f93b92.MirrorCS"),sQuery(id+"F2.wireOp",EDGE,"0b7ba8dc-1e88-4324-a412-ce5f49a3f93b94.MirrorCS"),sQuery(id+"F2.wireOp",EDGE,"0b7ba8dc-1e88-4324-a412-ce5f49a3f93b96.MirrorCS"),sQuery(id+"F2.wireOp",EDGE,"0b7ba8dc-1e88-4324-a412-ce5f49a3f93b99.MirrorCS"),sQuery(id+"F2.wireOp",EDGE,"0b7ba8dc-1e88-4324-a412-ce5f49a3f93b100.MirrorCS"),sQuery(id+"F2.wireOp",EDGE,"0b7ba8dc-1e88-4324-a412-ce5f49a3f93b101.MirrorCS"),sQuery(id+"F2.wireOp",EDGE,"0b7ba8dc-1e88-4324-a412-ce5f49a3f93b103.MirrorCS"),sQuery(id+"F2.wireOp",EDGE,"f0266a8e-7561-4b87-bd0b-eb2d287231cd103.MirrorCS"),sQuery(id+"F2.wireOp",EDGE,"f0266a8e-7561-4b87-bd0b-eb2d287231cd104.MirrorCS"),sQuery(id+"F2.wireOp",EDGE,"f0266a8e-7561-4b87-bd0b-eb2d287231cd105.MirrorCS"),sQuery(id+"F2.wireOp",EDGE,"f0266a8e-7561-4b87-bd0b-eb2d287231cd107.MirrorCS"),sQuery(id+"F2.wireOp",EDGE,"f0266a8e-7561-4b87-bd0b-eb2d287231cd111.MirrorCS"),sQuery(id+"F2.wireOp",EDGE,"f0266a8e-7561-4b87-bd0b-eb2d287231cd112.MirrorCS"),sQuery(id+"F2.wireOp",EDGE,"f0266a8e-7561-4b87-bd0b-eb2d287231cd114.MirrorCS"),sQuery(id+"F2.wireOp",EDGE,"f0266a8e-7561-4b87-bd0b-eb2d287231cd116.MirrorCS"),sQuery(id+"F2.wireOp",EDGE,"f0266a8e-7561-4b87-bd0b-eb2d287231cd118.MirrorCS"),sQuery(id+"F2.wireOp",EDGE,"f0266a8e-7561-4b87-bd0b-eb2d287231cd119.MirrorCS"),sQuery(id+"F2.wireOp",EDGE,"f0266a8e-7561-4b87-bd0b-eb2d287231cd120.MirrorCS"),sQuery(id+"F2.wireOp",EDGE,"f0266a8e-7561-4b87-bd0b-eb2d287231cd122.MirrorCS"),sQuery(id+"F2.wireOp",EDGE,"f0266a8e-7561-4b87-bd0b-eb2d287231cd123.MirrorCS"),sQuery(id+"F2.wireOp",EDGE,"f0266a8e-7561-4b87-bd0b-eb2d287231cd125.MirrorCS"),sQuery(id+"F2.wireOp",EDGE,"f0266a8e-7561-4b87-bd0b-eb2d287231cd127.MirrorCS"),sQuery(id+"F2.wireOp",EDGE,"f0266a8e-7561-4b87-bd0b-eb2d287231cd130.MirrorCS"),sQuery(id+"F2.wireOp",EDGE,"f0266a8e-7561-4b87-bd0b-eb2d287231cd132.MirrorCS"),sQuery(id+"F2.wireOp",EDGE,"f0266a8e-7561-4b87-bd0b-eb2d287231cd134.MirrorCS"),sQuery(id+"F2.wireOp",EDGE,"f0266a8e-7561-4b87-bd0b-eb2d287231cd137.MirrorCS"),sQuery(id+"F2.wireOp",EDGE,"f0266a8e-7561-4b87-bd0b-eb2d287231cd139.MirrorCS"),sQuery(id+"F2.wireOp",EDGE,"f0266a8e-7561-4b87-bd0b-eb2d287231cd145.MirrorCS"),sQuery(id+"F2.wireOp",EDGE,"f0266a8e-7561-4b87-bd0b-eb2d287231cd146.MirrorCS"),sQuery(id+"F2.wireOp",EDGE,"f0266a8e-7561-4b87-bd0b-eb2d287231cd148.MirrorCS"),sQuery(id+"F2.wireOp",EDGE,"f0266a8e-7561-4b87-bd0b-eb2d287231cd152.MirrorCS"),sQuery(id+"F2.wireOp",EDGE,"700fc68f-cb47-4a9b-971e-d9378dffceaa18.MirrorCS"),sQuery(id+"F2.wireOp",EDGE,"700fc68f-cb47-4a9b-971e-d9378dffceaa21.MirrorCS"),sQuery(id+"F2.wireOp",EDGE,"700fc68f-cb47-4a9b-971e-d9378dffceaa22.MirrorCS"),sQuery(id+"F2.wireOp",EDGE,"700fc68f-cb47-4a9b-971e-d9378dffceaa24.MirrorCS"),sQuery(id+"F2.wireOp",EDGE,"HybnvzRX-tT5h-yccU-n9Z5-Mlv0prX7MF2d.bottom")])],"isStart":false});
            var sketch = newSketch(context, id + "F5", { "sketchPlane" : qUnion([Q0])});
            skCircle(sketch, "E180", {"center": v(-68.26, 9.52) * mm, "radius": 1.5 * mm});
            skCircle(sketch, "E181.MirrorC", {"center": v(68.26, 9.52) * mm, "radius": 1.5 * mm});
            skCircle(sketch, "E182.MirrorC", {"center": v(-68.26, -9.52) * mm, "radius": 1.5 * mm});
            skCircle(sketch, "E183.MirrorC", {"center": v(68.26, -9.52) * mm, "radius": 1.5 * mm});
            skSolve(sketch);
        }
        {
            var Q0;
            Q0=qSketchRegion(id+"F5",true);
            extrude(context, id + "F6", {"entities" : qUnion([Q0]), "operationType" : NewBodyOperationType.REMOVE, "endBound" : BoundingType.THROUGH_ALL, "oppositeDirection" : true, "depth" : 25 * mm});
        }
        {
            var Q0;
            Q0=makeQuery(id+"F0.imprint","IMPRINT",FACE,{"disambiguationData":[TD([[makeQuery(id+"F0.imprint","IMPRINT",EDGE,{"derivedFrom":sQuery(id+"F0.wireOp",EDGE,"E3")}),-1.0]])]});
            var sketch = newSketch(context, id + "F7", { "sketchPlane" : qUnion([Q0])});
            skCircle(sketch, "E184", {"center": v(-8.04, -22.49) * mm, "radius": 8.5 * mm});
            skCircle(sketch, "E185", {"center": v(-8.04, -22.49) * mm, "radius": 6.2 * mm});
            skLineSegment(sketch, "E186", {"start": v(-8.04, -22.49) * mm, "end": v(-8.04, -16.29) * mm});
            skLineSegment(sketch, "E187.bottom", {"start": v(-7.3, -17.29) * mm, "end": v(-8.8, -17.29) * mm});
            skLineSegment(sketch, "E187.top", {"start": v(-7.3, -15.29) * mm, "end": v(-8.8, -15.29) * mm});
            skLineSegment(sketch, "E187.left", {"start": v(-7.3, -17.29) * mm, "end": v(-7.3, -15.29) * mm});
            skLineSegment(sketch, "E187.right", {"start": v(-8.8, -17.29) * mm, "end": v(-8.8, -15.29) * mm});
            skPoint(sketch, "E187.middle", {"position": v(-8.04, -16.29) * mm});
            skSolve(sketch);
        }
        {
            var Q0;
            Q0=qSketchRegion(id+"F7",true);
            var Q1;
            {var subQ1=sQuery(id+"F7.wireOp",EDGE,"E187.top");Q1=makeQuery(id+"F7.imprint","IMPRINT",FACE,{"disambiguationData":[TD([[makeQuery(id+"F7.imprint","IMPRINT",EDGE,{"derivedFrom":subQ1}),1.0]])]});}
            extrude(context, id + "F8", {"entities" : qUnion([Q0, Q1]), "operationType" : NewBodyOperationType.REMOVE, "depth" : 4 * mm});
        }
        {
            var Q0;
            Q0=makeQuery(id+"F3.opExtrude","CAP_FACE",FACE,{"disambiguationData":[OSD([sQuery(id+"F2.wireOp",EDGE,"E19"),sQuery(id+"F2.wireOp",EDGE,"E25"),sQuery(id+"F2.wireOp",EDGE,"E12"),sQuery(id+"F2.wireOp",EDGE,"E10"),sQuery(id+"F2.wireOp",EDGE,"E24"),sQuery(id+"F2.wireOp",EDGE,"E17"),sQuery(id+"F2.wireOp",EDGE,"E15"),sQuery(id+"F2.wireOp",EDGE,"E16"),sQuery(id+"F2.wireOp",EDGE,"E11"),sQuery(id+"F2.wireOp",EDGE,"E18"),sQuery(id+"F2.wireOp",EDGE,"E13"),sQuery(id+"F2.wireOp",EDGE,"E26"),sQuery(id+"F2.wireOp",EDGE,"E9"),sQuery(id+"F2.wireOp",EDGE,"E27"),sQuery(id+"F2.wireOp",EDGE,"E21"),sQuery(id+"F2.wireOp",EDGE,"E14"),sQuery(id+"F2.wireOp",EDGE,"E20"),sQuery(id+"F2.wireOp",EDGE,"E23"),sQuery(id+"F2.wireOp",EDGE,"E8"),sQuery(id+"F2.wireOp",EDGE,"E22"),sQuery(id+"F2.wireOp",EDGE,"vQyVyV5x-p2yk-mqKs-SuCr-8gVJOWqc7IX1"),sQuery(id+"F2.wireOp",EDGE,"E36.bottom"),sQuery(id+"F2.wireOp",EDGE,"E36.top"),sQuery(id+"F2.wireOp",EDGE,"E36.left"),sQuery(id+"F2.wireOp",EDGE,"E36.right"),sQuery(id+"F2.wireOp",EDGE,"E37.bottom"),sQuery(id+"F2.wireOp",EDGE,"E37.top"),sQuery(id+"F2.wireOp",EDGE,"E37.left"),sQuery(id+"F2.wireOp",EDGE,"E37.right"),sQuery(id+"F2.wireOp",EDGE,"7f746da5-9ad2-4a81-9fc8-e2dc20fbcc640.MirrorCS"),sQuery(id+"F2.wireOp",EDGE,"9dd7ed31-53ff-4210-8604-d896296ed41c0.MirrorCS"),sQuery(id+"F2.wireOp",EDGE,"c067bd87-fd3e-466a-810f-f065c564f8ed0.MirrorCS"),sQuery(id+"F2.wireOp",EDGE,"fd285260-f370-4225-87cf-36dfdc371af00.MirrorCS"),sQuery(id+"F2.wireOp",EDGE,"b8700096-e2a7-4ac0-8a1f-91fa73afae940.MirrorCS"),sQuery(id+"F2.wireOp",EDGE,"9a9e7c1c-7c8d-4d33-8a77-0f84e462b1150.MirrorCS"),sQuery(id+"F2.wireOp",EDGE,"c7a65c5f-7e80-4536-bd35-bc8f91e8c68b0.MirrorCS"),sQuery(id+"F2.wireOp",EDGE,"c29b3d01-277a-4ec0-8e36-8a23026f26020.MirrorCS"),sQuery(id+"F2.wireOp",EDGE,"0b7ba8dc-1e88-4324-a412-ce5f49a3f93b69.MirrorCS"),sQuery(id+"F2.wireOp",EDGE,"0b7ba8dc-1e88-4324-a412-ce5f49a3f93b71.MirrorCS"),sQuery(id+"F2.wireOp",EDGE,"0b7ba8dc-1e88-4324-a412-ce5f49a3f93b76.MirrorCS"),sQuery(id+"F2.wireOp",EDGE,"0b7ba8dc-1e88-4324-a412-ce5f49a3f93b78.MirrorCS"),sQuery(id+"F2.wireOp",EDGE,"0b7ba8dc-1e88-4324-a412-ce5f49a3f93b81.MirrorCS"),sQuery(id+"F2.wireOp",EDGE,"0b7ba8dc-1e88-4324-a412-ce5f49a3f93b82.MirrorCS"),sQuery(id+"F2.wireOp",EDGE,"0b7ba8dc-1e88-4324-a412-ce5f49a3f93b84.MirrorCS"),sQuery(id+"F2.wireOp",EDGE,"0b7ba8dc-1e88-4324-a412-ce5f49a3f93b86.MirrorCS"),sQuery(id+"F2.wireOp",EDGE,"0b7ba8dc-1e88-4324-a412-ce5f49a3f93b89.MirrorCS"),sQuery(id+"F2.wireOp",EDGE,"0b7ba8dc-1e88-4324-a412-ce5f49a3f93b92.MirrorCS"),sQuery(id+"F2.wireOp",EDGE,"0b7ba8dc-1e88-4324-a412-ce5f49a3f93b94.MirrorCS"),sQuery(id+"F2.wireOp",EDGE,"0b7ba8dc-1e88-4324-a412-ce5f49a3f93b96.MirrorCS"),sQuery(id+"F2.wireOp",EDGE,"0b7ba8dc-1e88-4324-a412-ce5f49a3f93b99.MirrorCS"),sQuery(id+"F2.wireOp",EDGE,"0b7ba8dc-1e88-4324-a412-ce5f49a3f93b100.MirrorCS"),sQuery(id+"F2.wireOp",EDGE,"0b7ba8dc-1e88-4324-a412-ce5f49a3f93b101.MirrorCS"),sQuery(id+"F2.wireOp",EDGE,"0b7ba8dc-1e88-4324-a412-ce5f49a3f93b103.MirrorCS"),sQuery(id+"F2.wireOp",EDGE,"f0266a8e-7561-4b87-bd0b-eb2d287231cd103.MirrorCS"),sQuery(id+"F2.wireOp",EDGE,"f0266a8e-7561-4b87-bd0b-eb2d287231cd104.MirrorCS"),sQuery(id+"F2.wireOp",EDGE,"f0266a8e-7561-4b87-bd0b-eb2d287231cd105.MirrorCS"),sQuery(id+"F2.wireOp",EDGE,"f0266a8e-7561-4b87-bd0b-eb2d287231cd107.MirrorCS"),sQuery(id+"F2.wireOp",EDGE,"f0266a8e-7561-4b87-bd0b-eb2d287231cd111.MirrorCS"),sQuery(id+"F2.wireOp",EDGE,"f0266a8e-7561-4b87-bd0b-eb2d287231cd112.MirrorCS"),sQuery(id+"F2.wireOp",EDGE,"f0266a8e-7561-4b87-bd0b-eb2d287231cd114.MirrorCS"),sQuery(id+"F2.wireOp",EDGE,"f0266a8e-7561-4b87-bd0b-eb2d287231cd116.MirrorCS"),sQuery(id+"F2.wireOp",EDGE,"f0266a8e-7561-4b87-bd0b-eb2d287231cd118.MirrorCS"),sQuery(id+"F2.wireOp",EDGE,"f0266a8e-7561-4b87-bd0b-eb2d287231cd119.MirrorCS"),sQuery(id+"F2.wireOp",EDGE,"f0266a8e-7561-4b87-bd0b-eb2d287231cd120.MirrorCS"),sQuery(id+"F2.wireOp",EDGE,"f0266a8e-7561-4b87-bd0b-eb2d287231cd122.MirrorCS"),sQuery(id+"F2.wireOp",EDGE,"f0266a8e-7561-4b87-bd0b-eb2d287231cd123.MirrorCS"),sQuery(id+"F2.wireOp",EDGE,"f0266a8e-7561-4b87-bd0b-eb2d287231cd125.MirrorCS"),sQuery(id+"F2.wireOp",EDGE,"f0266a8e-7561-4b87-bd0b-eb2d287231cd127.MirrorCS"),sQuery(id+"F2.wireOp",EDGE,"f0266a8e-7561-4b87-bd0b-eb2d287231cd130.MirrorCS"),sQuery(id+"F2.wireOp",EDGE,"f0266a8e-7561-4b87-bd0b-eb2d287231cd132.MirrorCS"),sQuery(id+"F2.wireOp",EDGE,"f0266a8e-7561-4b87-bd0b-eb2d287231cd134.MirrorCS"),sQuery(id+"F2.wireOp",EDGE,"f0266a8e-7561-4b87-bd0b-eb2d287231cd137.MirrorCS"),sQuery(id+"F2.wireOp",EDGE,"f0266a8e-7561-4b87-bd0b-eb2d287231cd139.MirrorCS"),sQuery(id+"F2.wireOp",EDGE,"f0266a8e-7561-4b87-bd0b-eb2d287231cd145.MirrorCS"),sQuery(id+"F2.wireOp",EDGE,"f0266a8e-7561-4b87-bd0b-eb2d287231cd146.MirrorCS"),sQuery(id+"F2.wireOp",EDGE,"f0266a8e-7561-4b87-bd0b-eb2d287231cd148.MirrorCS"),sQuery(id+"F2.wireOp",EDGE,"f0266a8e-7561-4b87-bd0b-eb2d287231cd152.MirrorCS"),sQuery(id+"F2.wireOp",EDGE,"700fc68f-cb47-4a9b-971e-d9378dffceaa18.MirrorCS"),sQuery(id+"F2.wireOp",EDGE,"700fc68f-cb47-4a9b-971e-d9378dffceaa21.MirrorCS"),sQuery(id+"F2.wireOp",EDGE,"700fc68f-cb47-4a9b-971e-d9378dffceaa22.MirrorCS"),sQuery(id+"F2.wireOp",EDGE,"700fc68f-cb47-4a9b-971e-d9378dffceaa24.MirrorCS"),sQuery(id+"F2.wireOp",EDGE,"HybnvzRX-tT5h-yccU-n9Z5-Mlv0prX7MF2d.bottom")])],"isStart":false});
            var sketch = newSketch(context, id + "F9", { "sketchPlane" : qUnion([Q0])});
            skSolve(sketch);
        }
        {
            var Q0;
            {var subQ81=sQuery(id+"F2.wireOp",EDGE,"E10");Q0=makeQuery(id+"F9.imprint","IMPRINT",FACE,{"disambiguationData":[TD([[makeQuery(id+"F9.imprint","IMPRINT",EDGE,{"derivedFrom":makeQuery(id+"F3.opExtrude","CAP_EDGE",EDGE,{"disambiguationData":[OSD([subQ81])],"isStart":false})}),-1.0]])]});}
            var sketch = newSketch(context, id + "F10", { "sketchPlane" : qUnion([Q0])});
            skLineSegment(sketch, "E188.bottom", {"start": v(43.48, 16.77) * mm, "end": v(0.55, 16.77) * mm});
            skLineSegment(sketch, "E188.top", {"start": v(43.48, 28.2) * mm, "end": v(0.55, 28.2) * mm});
            skLineSegment(sketch, "E188.left", {"start": v(43.48, 16.77) * mm, "end": v(43.48, 28.2) * mm});
            skLineSegment(sketch, "E188.right", {"start": v(0.55, 16.77) * mm, "end": v(0.55, 28.2) * mm});
            skPoint(sketch, "E188.middle", {"position": v(22.01, 22.49) * mm});
            skLineSegment(sketch, "E189.MirrorCS", {"start": v(43.48, -16.77) * mm, "end": v(0.55, -16.77) * mm});
            skLineSegment(sketch, "E190.MirrorCS", {"start": v(43.48, -28.2) * mm, "end": v(0.55, -28.2) * mm});
            skLineSegment(sketch, "E191.MirrorCS", {"start": v(0.55, -16.77) * mm, "end": v(0.55, -28.2) * mm});
            skLineSegment(sketch, "E192.MirrorCS", {"start": v(43.48, -16.77) * mm, "end": v(43.48, -28.2) * mm});
            skLineSegment(sketch, "E193.bottom", {"start": v(43.48, 13.21) * mm, "end": v(0.55, 13.21) * mm});
            skLineSegment(sketch, "E193.top", {"start": v(43.48, 1.78) * mm, "end": v(0.55, 1.78) * mm});
            skLineSegment(sketch, "E193.left", {"start": v(43.48, 13.21) * mm, "end": v(43.48, 1.78) * mm});
            skLineSegment(sketch, "E193.right", {"start": v(0.55, 13.21) * mm, "end": v(0.55, 1.78) * mm});
            skPoint(sketch, "E193.middle", {"position": v(22.01, 7.5) * mm});
            skLineSegment(sketch, "E194.MirrorCS", {"start": v(43.48, -1.78) * mm, "end": v(0.55, -1.78) * mm});
            skLineSegment(sketch, "E195.MirrorCS", {"start": v(0.55, -13.21) * mm, "end": v(0.55, -1.78) * mm});
            skLineSegment(sketch, "E196.MirrorCS", {"start": v(43.48, -13.21) * mm, "end": v(0.55, -13.21) * mm});
            skLineSegment(sketch, "E197.MirrorCS", {"start": v(43.48, -13.21) * mm, "end": v(43.48, -1.78) * mm});
            skLineSegment(sketch, "E198.bottom", {"start": v(0.55, 10) * mm, "end": v(43.48, 10) * mm});
            skLineSegment(sketch, "E198.top", {"start": v(0.55, 5) * mm, "end": v(43.48, 5) * mm});
            skLineSegment(sketch, "E198.left", {"start": v(0.55, 10) * mm, "end": v(0.55, 5) * mm});
            skLineSegment(sketch, "E198.right", {"start": v(43.48, 10) * mm, "end": v(43.48, 5) * mm});
            skLineSegment(sketch, "E199.MirrorCS", {"start": v(0.55, -10) * mm, "end": v(43.48, -10) * mm});
            skLineSegment(sketch, "E200.MirrorCS", {"start": v(0.55, -5) * mm, "end": v(43.48, -5) * mm});
            skLineSegment(sketch, "E201.bottom", {"start": v(0.55, 24.99) * mm, "end": v(43.48, 24.99) * mm});
            skLineSegment(sketch, "E201.top", {"start": v(0.55, 19.99) * mm, "end": v(43.48, 19.99) * mm});
            skLineSegment(sketch, "E201.left", {"start": v(0.55, 24.99) * mm, "end": v(0.55, 19.99) * mm});
            skLineSegment(sketch, "E201.right", {"start": v(43.48, 24.99) * mm, "end": v(43.48, 19.99) * mm});
            skLineSegment(sketch, "E202.MirrorCS", {"start": v(0.55, -24.99) * mm, "end": v(43.48, -24.99) * mm});
            skLineSegment(sketch, "E203.MirrorCS", {"start": v(0.55, -19.99) * mm, "end": v(43.48, -19.99) * mm});
            skPoint(sketch, "E204", {"position": v(52.01, 22.49) * mm});
            skPoint(sketch, "E205", {"position": v(52.01, 7.5) * mm});
            skPoint(sketch, "E205.positionSnap0", {"position": v(43.48, 7.5) * mm});
            skPoint(sketch, "E206", {"position": v(52.01, -7.5) * mm});
            skPoint(sketch, "E206.positionSnap0", {"position": v(43.48, -7.5) * mm});
            skPoint(sketch, "E207", {"position": v(52.01, -22.49) * mm});
            skPoint(sketch, "E207.positionSnap0", {"position": v(43.48, -22.49) * mm});
            skSolve(sketch);
        }
        {
            var Q0;
            Q0=makeQuery(id+"F10.imprint","IMPRINT",FACE,{"disambiguationData":[TD([[makeQuery(id+"F10.imprint","IMPRINT",EDGE,{"derivedFrom":sQuery(id+"F10.wireOp",EDGE,"E188.bottom")}),-1.0]])]});
            var Q1;
            Q1=makeQuery(id+"F10.imprint","IMPRINT",FACE,{"disambiguationData":[TD([[makeQuery(id+"F10.imprint","IMPRINT",EDGE,{"derivedFrom":sQuery(id+"F10.wireOp",EDGE,"E193.bottom")}),1.0]])]});
            var Q2;
            Q2=makeQuery(id+"F10.imprint","IMPRINT",FACE,{"disambiguationData":[TD([[makeQuery(id+"F10.imprint","IMPRINT",EDGE,{"derivedFrom":sQuery(id+"F10.wireOp",EDGE,"E194.MirrorCS")}),1.0]])]});
            var Q3;
            Q3=makeQuery(id+"F10.imprint","IMPRINT",FACE,{"disambiguationData":[TD([[makeQuery(id+"F10.imprint","IMPRINT",EDGE,{"derivedFrom":sQuery(id+"F10.wireOp",EDGE,"E189.MirrorCS")}),1.0]])]});
            var Q4;
            Q4=makeQuery(id+"F10.imprint","IMPRINT",FACE,{"disambiguationData":[TD([[makeQuery(id+"F10.imprint","IMPRINT",EDGE,{"derivedFrom":sQuery(id+"F10.wireOp",EDGE,"E201.bottom")}),-1.0]])]});
            var Q5;
            {var subQ0=sQuery(id+"F10.wireOp",EDGE,"E188.top");Q5=makeQuery(id+"F10.imprint","IMPRINT",FACE,{"disambiguationData":[TD([[makeQuery(id+"F10.imprint","IMPRINT",EDGE,{"derivedFrom":subQ0}),1.0]])]});}
            var Q6;
            Q6=makeQuery(id+"F10.imprint","IMPRINT",FACE,{"disambiguationData":[TD([[makeQuery(id+"F10.imprint","IMPRINT",EDGE,{"derivedFrom":sQuery(id+"F10.wireOp",EDGE,"E198.bottom")}),-1.0]])]});
            var Q7;
            {var subQ0=sQuery(id+"F10.wireOp",EDGE,"E193.top");Q7=makeQuery(id+"F10.imprint","IMPRINT",FACE,{"disambiguationData":[TD([[makeQuery(id+"F10.imprint","IMPRINT",EDGE,{"derivedFrom":subQ0}),-1.0]])]});}
            var Q8;
            {var subQ0=sQuery(id+"F10.wireOp",EDGE,"E199.MirrorCS");Q8=makeQuery(id+"F10.imprint","IMPRINT",FACE,{"disambiguationData":[TD([[makeQuery(id+"F10.imprint","IMPRINT",EDGE,{"derivedFrom":subQ0}),1.0]])]});}
            var Q9;
            {var subQ0=sQuery(id+"F10.wireOp",EDGE,"E196.MirrorCS");Q9=makeQuery(id+"F10.imprint","IMPRINT",FACE,{"disambiguationData":[TD([[makeQuery(id+"F10.imprint","IMPRINT",EDGE,{"derivedFrom":subQ0}),-1.0]])]});}
            var Q10;
            {var subQ0=sQuery(id+"F10.wireOp",EDGE,"E190.MirrorCS");Q10=makeQuery(id+"F10.imprint","IMPRINT",FACE,{"disambiguationData":[TD([[makeQuery(id+"F10.imprint","IMPRINT",EDGE,{"derivedFrom":subQ0}),-1.0]])]});}
            var Q11;
            {var subQ0=sQuery(id+"F10.wireOp",EDGE,"E202.MirrorCS");Q11=makeQuery(id+"F10.imprint","IMPRINT",FACE,{"disambiguationData":[TD([[makeQuery(id+"F10.imprint","IMPRINT",EDGE,{"derivedFrom":subQ0}),1.0]])]});}
            extrude(context, id + "F11", {"entities" : qUnion([Q0, Q1, Q2, Q3, Q4, Q5, Q6, Q7, Q8, Q9, Q10, Q11]), "operationType" : NewBodyOperationType.REMOVE, "oppositeDirection" : true, "depth" : 8 * mm});
        }
        {
            var Q0;
            {var subQ0=sQuery(id+"F10.wireOp",EDGE,"E189.MirrorCS");Q0=makeQuery(id+"F10.imprint","IMPRINT",FACE,{"disambiguationData":[TD([[makeQuery(id+"F10.imprint","IMPRINT",EDGE,{"derivedFrom":subQ0}),1.0]])]});}
            var Q1;
            {var subQ0=sQuery(id+"F10.wireOp",EDGE,"E190.MirrorCS");Q1=makeQuery(id+"F10.imprint","IMPRINT",FACE,{"disambiguationData":[TD([[makeQuery(id+"F10.imprint","IMPRINT",EDGE,{"derivedFrom":subQ0}),-1.0]])]});}
            var Q2;
            {var subQ0=sQuery(id+"F10.wireOp",EDGE,"E196.MirrorCS");Q2=makeQuery(id+"F10.imprint","IMPRINT",FACE,{"disambiguationData":[TD([[makeQuery(id+"F10.imprint","IMPRINT",EDGE,{"derivedFrom":subQ0}),-1.0]])]});}
            var Q3;
            {var subQ0=sQuery(id+"F10.wireOp",EDGE,"E193.top");Q3=makeQuery(id+"F10.imprint","IMPRINT",FACE,{"disambiguationData":[TD([[makeQuery(id+"F10.imprint","IMPRINT",EDGE,{"derivedFrom":subQ0}),-1.0]])]});}
            var Q4;
            {var subQ0=sQuery(id+"F10.wireOp",EDGE,"E194.MirrorCS");Q4=makeQuery(id+"F10.imprint","IMPRINT",FACE,{"disambiguationData":[TD([[makeQuery(id+"F10.imprint","IMPRINT",EDGE,{"derivedFrom":subQ0}),1.0]])]});}
            var Q5;
            {var subQ0=sQuery(id+"F10.wireOp",EDGE,"E193.bottom");Q5=makeQuery(id+"F10.imprint","IMPRINT",FACE,{"disambiguationData":[TD([[makeQuery(id+"F10.imprint","IMPRINT",EDGE,{"derivedFrom":subQ0}),1.0]])]});}
            var Q6;
            {var subQ0=sQuery(id+"F10.wireOp",EDGE,"E188.bottom");Q6=makeQuery(id+"F10.imprint","IMPRINT",FACE,{"disambiguationData":[TD([[makeQuery(id+"F10.imprint","IMPRINT",EDGE,{"derivedFrom":subQ0}),-1.0]])]});}
            var Q7;
            {var subQ0=sQuery(id+"F10.wireOp",EDGE,"E188.top");Q7=makeQuery(id+"F10.imprint","IMPRINT",FACE,{"disambiguationData":[TD([[makeQuery(id+"F10.imprint","IMPRINT",EDGE,{"derivedFrom":subQ0}),1.0]])]});}
            extrude(context, id + "F12", {"entities" : qUnion([Q0, Q1, Q2, Q3, Q4, Q5, Q6, Q7]), "operationType" : NewBodyOperationType.REMOVE, "oppositeDirection" : true, "depth" : 25 * mm});
        }
        {
            var Q0;
            {var subQ5=sQuery(id+"F2.wireOp",EDGE,"E49.MirrorCS");Q0=makeQuery(id+"F2.imprint","IMPRINT",FACE,{"disambiguationData":[TD([[makeQuery(id+"F2.imprint","IMPRINT",EDGE,{"derivedFrom":subQ5}),-1.0]])]});}
            var Q1;
            {var subQ0=sQuery(id+"F2.wireOp",EDGE,"E55.MirrorCS");Q1=makeQuery(id+"F2.imprint","IMPRINT",FACE,{"disambiguationData":[TD([[makeQuery(id+"F2.imprint","IMPRINT",EDGE,{"derivedFrom":subQ0}),1.0]])]});}
            var Q2;
            {var subQ1=sQuery(id+"F2.wireOp",EDGE,"E64.MirrorCS");Q2=makeQuery(id+"F2.imprint","IMPRINT",FACE,{"disambiguationData":[TD([[makeQuery(id+"F2.imprint","IMPRINT",EDGE,{"derivedFrom":subQ1}),-1.0]])]});}
            var Q3;
            {var subQ0=sQuery(id+"F2.wireOp",EDGE,"E61.MirrorCS");Q3=makeQuery(id+"F2.imprint","IMPRINT",FACE,{"disambiguationData":[TD([[makeQuery(id+"F2.imprint","IMPRINT",EDGE,{"derivedFrom":subQ0}),1.0]])]});}
            var Q4;
            {var subQ1=sQuery(id+"F2.wireOp",EDGE,"E47.top");Q4=makeQuery(id+"F2.imprint","IMPRINT",FACE,{"disambiguationData":[TD([[makeQuery(id+"F2.imprint","IMPRINT",EDGE,{"derivedFrom":subQ1}),-1.0]])]});}
            var Q5;
            {var subQ0=sQuery(id+"F2.wireOp",EDGE,"E75.MirrorCS");Q5=makeQuery(id+"F2.imprint","IMPRINT",FACE,{"disambiguationData":[TD([[makeQuery(id+"F2.imprint","IMPRINT",EDGE,{"derivedFrom":subQ0}),1.0]])]});}
            var Q6;
            {var subQ4=sQuery(id+"F2.wireOp",EDGE,"E68.MirrorCS");Q6=makeQuery(id+"F2.imprint","IMPRINT",FACE,{"disambiguationData":[TD([[makeQuery(id+"F2.imprint","IMPRINT",EDGE,{"derivedFrom":subQ4}),-1.0]])]});}
            var Q7;
            {var subQ1=sQuery(id+"F2.wireOp",EDGE,"E71.MirrorCS");Q7=makeQuery(id+"F2.imprint","IMPRINT",FACE,{"disambiguationData":[TD([[makeQuery(id+"F2.imprint","IMPRINT",EDGE,{"derivedFrom":subQ1}),1.0]])]});}
            var Q8;
            {var subQ8=sQuery(id+"F2.wireOp",EDGE,"E103.MirrorCS");Q8=makeQuery(id+"F2.imprint","IMPRINT",FACE,{"disambiguationData":[TD([[makeQuery(id+"F2.imprint","IMPRINT",EDGE,{"derivedFrom":subQ8}),-1.0]])]});}
            var Q9;
            {var subQ1=sQuery(id+"F2.wireOp",EDGE,"E116.MirrorCS");Q9=makeQuery(id+"F2.imprint","IMPRINT",FACE,{"disambiguationData":[TD([[makeQuery(id+"F2.imprint","IMPRINT",EDGE,{"derivedFrom":subQ1}),1.0]])]});}
            var Q10;
            {var subQ0=sQuery(id+"F2.wireOp",EDGE,"E117.MirrorCS");Q10=makeQuery(id+"F2.imprint","IMPRINT",FACE,{"disambiguationData":[TD([[makeQuery(id+"F2.imprint","IMPRINT",EDGE,{"derivedFrom":subQ0}),-1.0]])]});}
            var Q11;
            {var subQ1=sQuery(id+"F2.wireOp",EDGE,"E102.MirrorCS");Q11=makeQuery(id+"F2.imprint","IMPRINT",FACE,{"disambiguationData":[TD([[makeQuery(id+"F2.imprint","IMPRINT",EDGE,{"derivedFrom":subQ1}),1.0]])]});}
            var Q12;
            Q12=makeQuery(id+"F2.imprint","IMPRINT",FACE,{"disambiguationData":[TD([[makeQuery(id+"F2.imprint","IMPRINT",EDGE,{"derivedFrom":sQuery(id+"F2.wireOp",EDGE,"E113.MirrorCS")}),1.0]])]});
            var Q13;
            {var subQ4=sQuery(id+"F2.wireOp",EDGE,"E97.MirrorCS");Q13=makeQuery(id+"F2.imprint","IMPRINT",FACE,{"disambiguationData":[TD([[makeQuery(id+"F2.imprint","IMPRINT",EDGE,{"derivedFrom":subQ4}),1.0]])]});}
            var Q14;
            {var subQ1=sQuery(id+"F2.wireOp",EDGE,"E106.MirrorCS");Q14=makeQuery(id+"F2.imprint","IMPRINT",FACE,{"disambiguationData":[TD([[makeQuery(id+"F2.imprint","IMPRINT",EDGE,{"derivedFrom":subQ1}),-1.0]])]});}
            extrude(context, id + "F13", {"entities" : qUnion([Q0, Q1, Q2, Q3, Q4, Q5, Q6, Q7, Q8, Q9, Q10, Q11, Q12, Q13, Q14]), "operationType" : NewBodyOperationType.REMOVE, "oppositeDirection" : true, "depth" : 25 * mm});
        }
        {
            var Q0;
            Q0=makeQuery(id+"F7.imprint","IMPRINT",FACE,{"disambiguationData":[TD([[makeQuery(id+"F7.imprint","IMPRINT",EDGE,{"derivedFrom":sQuery(id+"F7.wireOp",EDGE,"E185")}),1.0]])]});
            extrude(context, id + "F14", {"entities" : qUnion([Q0]), "operationType" : NewBodyOperationType.REMOVE, "depth" : 25 * mm, "symmetric" : true});
        }
        {
            var Q0;
            Q0=sQuery(id+"F10.wireOp",VERTEX,"E204");
            var Q1;
            Q1=sQuery(id+"F10.wireOp",VERTEX,"E205");
            var Q2;
            Q2=sQuery(id+"F10.wireOp",VERTEX,"E207");
            var Q3;
            Q3=sQuery(id+"F10.wireOp",VERTEX,"E206");
            var Q4;
            Q4=makeQuery(id+"F1.opExtrude","SWEPT_BODY",BODY,{"disambiguationData":[OSD([sQuery(id+"F0.wireOp",EDGE,"E3"),sQuery(id+"F0.wireOp",EDGE,"E4"),sQuery(id+"F0.wireOp",EDGE,"E2"),sQuery(id+"F0.wireOp",EDGE,"E5"),sQuery(id+"F0.wireOp",EDGE,"E0"),sQuery(id+"F0.wireOp",EDGE,"E1"),sQuery(id+"F0.wireOp",EDGE,"E6"),sQuery(id+"F0.wireOp",EDGE,"E7")])]});
            var Q5;
            Q5=makeQuery(id+"F3.opExtrude","SWEPT_BODY",BODY,{"disambiguationData":[OSD([sQuery(id+"F2.wireOp",EDGE,"E19"),sQuery(id+"F2.wireOp",EDGE,"E25"),sQuery(id+"F2.wireOp",EDGE,"E12"),sQuery(id+"F2.wireOp",EDGE,"E10"),sQuery(id+"F2.wireOp",EDGE,"E24"),sQuery(id+"F2.wireOp",EDGE,"E17"),sQuery(id+"F2.wireOp",EDGE,"E15"),sQuery(id+"F2.wireOp",EDGE,"E16"),sQuery(id+"F2.wireOp",EDGE,"E11"),sQuery(id+"F2.wireOp",EDGE,"E18"),sQuery(id+"F2.wireOp",EDGE,"E13"),sQuery(id+"F2.wireOp",EDGE,"E26"),sQuery(id+"F2.wireOp",EDGE,"E9"),sQuery(id+"F2.wireOp",EDGE,"E27"),sQuery(id+"F2.wireOp",EDGE,"E21"),sQuery(id+"F2.wireOp",EDGE,"E14"),sQuery(id+"F2.wireOp",EDGE,"E20"),sQuery(id+"F2.wireOp",EDGE,"E23"),sQuery(id+"F2.wireOp",EDGE,"E8"),sQuery(id+"F2.wireOp",EDGE,"E22"),sQuery(id+"F2.wireOp",EDGE,"E47.bottom"),sQuery(id+"F2.wireOp",EDGE,"E47.top"),sQuery(id+"F2.wireOp",EDGE,"E47.left"),sQuery(id+"F2.wireOp",EDGE,"E47.right"),sQuery(id+"F2.wireOp",EDGE,"E48.MirrorCS"),sQuery(id+"F2.wireOp",EDGE,"E49.MirrorCS"),sQuery(id+"F2.wireOp",EDGE,"E50.MirrorCS"),sQuery(id+"F2.wireOp",EDGE,"E51.MirrorCS"),sQuery(id+"F2.wireOp",EDGE,"E52.MirrorCS"),sQuery(id+"F2.wireOp",EDGE,"E53.MirrorCS"),sQuery(id+"F2.wireOp",EDGE,"E54.MirrorCS"),sQuery(id+"F2.wireOp",EDGE,"E55.MirrorCS"),sQuery(id+"F2.wireOp",EDGE,"E58.MirrorCS"),sQuery(id+"F2.wireOp",EDGE,"E59.MirrorCS"),sQuery(id+"F2.wireOp",EDGE,"E60.MirrorCS"),sQuery(id+"F2.wireOp",EDGE,"E61.MirrorCS"),sQuery(id+"F2.wireOp",EDGE,"E62.MirrorCS"),sQuery(id+"F2.wireOp",EDGE,"E63.MirrorCS"),sQuery(id+"F2.wireOp",EDGE,"E64.MirrorCS"),sQuery(id+"F2.wireOp",EDGE,"E57.MirrorCS"),sQuery(id+"F2.wireOp",EDGE,"E65.MirrorCS"),sQuery(id+"F2.wireOp",EDGE,"E67.MirrorCS"),sQuery(id+"F2.wireOp",EDGE,"E68.MirrorCS"),sQuery(id+"F2.wireOp",EDGE,"E70.MirrorCS"),sQuery(id+"F2.wireOp",EDGE,"E71.MirrorCS"),sQuery(id+"F2.wireOp",EDGE,"E72.MirrorCS"),sQuery(id+"F2.wireOp",EDGE,"E73.MirrorCS"),sQuery(id+"F2.wireOp",EDGE,"E74.MirrorCS"),sQuery(id+"F2.wireOp",EDGE,"E75.MirrorCS"),sQuery(id+"F2.wireOp",EDGE,"E76.MirrorCS"),sQuery(id+"F2.wireOp",EDGE,"E77.MirrorCS"),sQuery(id+"F2.wireOp",EDGE,"E79.MirrorCS"),sQuery(id+"F2.wireOp",EDGE,"E92.MirrorCS"),sQuery(id+"F2.wireOp",EDGE,"E96.MirrorCS"),sQuery(id+"F2.wireOp",EDGE,"E97.MirrorCS"),sQuery(id+"F2.wireOp",EDGE,"E98.MirrorCS"),sQuery(id+"F2.wireOp",EDGE,"E99.MirrorCS"),sQuery(id+"F2.wireOp",EDGE,"E100.MirrorCS"),sQuery(id+"F2.wireOp",EDGE,"E101.MirrorCS"),sQuery(id+"F2.wireOp",EDGE,"E102.MirrorCS"),sQuery(id+"F2.wireOp",EDGE,"E87.MirrorCS"),sQuery(id+"F2.wireOp",EDGE,"E103.MirrorCS"),sQuery(id+"F2.wireOp",EDGE,"E83.MirrorCS"),sQuery(id+"F2.wireOp",EDGE,"E104.MirrorCS"),sQuery(id+"F2.wireOp",EDGE,"E105.MirrorCS"),sQuery(id+"F2.wireOp",EDGE,"E106.MirrorCS"),sQuery(id+"F2.wireOp",EDGE,"E107.MirrorCS"),sQuery(id+"F2.wireOp",EDGE,"E108.MirrorCS"),sQuery(id+"F2.wireOp",EDGE,"E109.MirrorCS"),sQuery(id+"F2.wireOp",EDGE,"E110.MirrorCS"),sQuery(id+"F2.wireOp",EDGE,"E111.MirrorCS"),sQuery(id+"F2.wireOp",EDGE,"E112.MirrorCS"),sQuery(id+"F2.wireOp",EDGE,"E113.MirrorCS"),sQuery(id+"F2.wireOp",EDGE,"E114.MirrorCS"),sQuery(id+"F2.wireOp",EDGE,"E115.MirrorCS"),sQuery(id+"F2.wireOp",EDGE,"E116.MirrorCS"),sQuery(id+"F2.wireOp",EDGE,"E117.MirrorCS"),sQuery(id+"F2.wireOp",EDGE,"E118.MirrorCS"),sQuery(id+"F2.wireOp",EDGE,"E121.MirrorCS"),sQuery(id+"F2.wireOp",EDGE,"E122.MirrorCS"),sQuery(id+"F2.wireOp",EDGE,"E123.bottom"),sQuery(id+"F2.wireOp",EDGE,"E123.left"),sQuery(id+"F2.wireOp",EDGE,"E138.bottom"),sQuery(id+"F2.wireOp",EDGE,"E138.left"),sQuery(id+"F2.wireOp",EDGE,"E153.bottom"),sQuery(id+"F2.wireOp",EDGE,"E153.left"),sQuery(id+"F2.wireOp",EDGE,"E169.bottom"),sQuery(id+"F2.wireOp",EDGE,"E169.left")])]});
            hole(context, id + "F15", {"style" : HoleStyle.SIMPLE, "endStyle" : HoleEndStyle.THROUGH, "holeDiameter" : 7 * mm, "isTappedThrough" : true, "tappedDepth" : 12 * mm, "tapClearance" : 3, "locations" : qUnion([Q0, Q1, Q2, Q3]), "scope" : qUnion([Q4, Q5])});
        }
        {
            var Q0;
            Q0=makeQuery(id+"F2.imprint","IMPRINT",FACE,{"disambiguationData":[TD([[makeQuery(id+"F2.imprint","IMPRINT",EDGE,{"derivedFrom":sQuery(id+"F2.wireOp",EDGE,"E19")}),1.0]])]});
            var sketch = newSketch(context, id + "F16", { "sketchPlane" : qUnion([Q0])});
            skPoint(sketch, "E208", {"position": v(52.01, 22.49) * mm});
            skPoint(sketch, "E209", {"position": v(52.01, 7.5) * mm});
            skPoint(sketch, "E210.MirrorP", {"position": v(52.01, -7.5) * mm});
            skPoint(sketch, "E211.MirrorP", {"position": v(52.01, -22.49) * mm});
            skSolve(sketch);
        }
        {
            var Q0;
            Q0=sQuery(id+"F16.wireOp",VERTEX,"E208");
            var Q1;
            Q1=sQuery(id+"F16.wireOp",VERTEX,"E209");
            var Q2;
            Q2=sQuery(id+"F16.wireOp",VERTEX,"E210.MirrorP");
            var Q3;
            Q3=sQuery(id+"F16.wireOp",VERTEX,"E211.MirrorP");
            var Q4;
            Q4=makeQuery(id+"F3.opExtrude","SWEPT_BODY",BODY,{"disambiguationData":[OSD([sQuery(id+"F2.wireOp",EDGE,"E19"),sQuery(id+"F2.wireOp",EDGE,"E25"),sQuery(id+"F2.wireOp",EDGE,"E12"),sQuery(id+"F2.wireOp",EDGE,"E10"),sQuery(id+"F2.wireOp",EDGE,"E24"),sQuery(id+"F2.wireOp",EDGE,"E17"),sQuery(id+"F2.wireOp",EDGE,"E15"),sQuery(id+"F2.wireOp",EDGE,"E16"),sQuery(id+"F2.wireOp",EDGE,"E11"),sQuery(id+"F2.wireOp",EDGE,"E18"),sQuery(id+"F2.wireOp",EDGE,"E13"),sQuery(id+"F2.wireOp",EDGE,"E26"),sQuery(id+"F2.wireOp",EDGE,"E9"),sQuery(id+"F2.wireOp",EDGE,"E27"),sQuery(id+"F2.wireOp",EDGE,"E21"),sQuery(id+"F2.wireOp",EDGE,"E14"),sQuery(id+"F2.wireOp",EDGE,"E20"),sQuery(id+"F2.wireOp",EDGE,"E23"),sQuery(id+"F2.wireOp",EDGE,"E8"),sQuery(id+"F2.wireOp",EDGE,"E22"),sQuery(id+"F2.wireOp",EDGE,"E47.bottom"),sQuery(id+"F2.wireOp",EDGE,"E47.top"),sQuery(id+"F2.wireOp",EDGE,"E47.left"),sQuery(id+"F2.wireOp",EDGE,"E47.right"),sQuery(id+"F2.wireOp",EDGE,"E48.MirrorCS"),sQuery(id+"F2.wireOp",EDGE,"E49.MirrorCS"),sQuery(id+"F2.wireOp",EDGE,"E50.MirrorCS"),sQuery(id+"F2.wireOp",EDGE,"E51.MirrorCS"),sQuery(id+"F2.wireOp",EDGE,"E52.MirrorCS"),sQuery(id+"F2.wireOp",EDGE,"E53.MirrorCS"),sQuery(id+"F2.wireOp",EDGE,"E54.MirrorCS"),sQuery(id+"F2.wireOp",EDGE,"E55.MirrorCS"),sQuery(id+"F2.wireOp",EDGE,"E58.MirrorCS"),sQuery(id+"F2.wireOp",EDGE,"E59.MirrorCS"),sQuery(id+"F2.wireOp",EDGE,"E60.MirrorCS"),sQuery(id+"F2.wireOp",EDGE,"E61.MirrorCS"),sQuery(id+"F2.wireOp",EDGE,"E62.MirrorCS"),sQuery(id+"F2.wireOp",EDGE,"E63.MirrorCS"),sQuery(id+"F2.wireOp",EDGE,"E64.MirrorCS"),sQuery(id+"F2.wireOp",EDGE,"E57.MirrorCS"),sQuery(id+"F2.wireOp",EDGE,"E65.MirrorCS"),sQuery(id+"F2.wireOp",EDGE,"E67.MirrorCS"),sQuery(id+"F2.wireOp",EDGE,"E68.MirrorCS"),sQuery(id+"F2.wireOp",EDGE,"E70.MirrorCS"),sQuery(id+"F2.wireOp",EDGE,"E71.MirrorCS"),sQuery(id+"F2.wireOp",EDGE,"E72.MirrorCS"),sQuery(id+"F2.wireOp",EDGE,"E73.MirrorCS"),sQuery(id+"F2.wireOp",EDGE,"E74.MirrorCS"),sQuery(id+"F2.wireOp",EDGE,"E75.MirrorCS"),sQuery(id+"F2.wireOp",EDGE,"E76.MirrorCS"),sQuery(id+"F2.wireOp",EDGE,"E77.MirrorCS"),sQuery(id+"F2.wireOp",EDGE,"E79.MirrorCS"),sQuery(id+"F2.wireOp",EDGE,"E92.MirrorCS"),sQuery(id+"F2.wireOp",EDGE,"E96.MirrorCS"),sQuery(id+"F2.wireOp",EDGE,"E97.MirrorCS"),sQuery(id+"F2.wireOp",EDGE,"E98.MirrorCS"),sQuery(id+"F2.wireOp",EDGE,"E99.MirrorCS"),sQuery(id+"F2.wireOp",EDGE,"E100.MirrorCS"),sQuery(id+"F2.wireOp",EDGE,"E101.MirrorCS"),sQuery(id+"F2.wireOp",EDGE,"E102.MirrorCS"),sQuery(id+"F2.wireOp",EDGE,"E87.MirrorCS"),sQuery(id+"F2.wireOp",EDGE,"E103.MirrorCS"),sQuery(id+"F2.wireOp",EDGE,"E83.MirrorCS"),sQuery(id+"F2.wireOp",EDGE,"E104.MirrorCS"),sQuery(id+"F2.wireOp",EDGE,"E105.MirrorCS"),sQuery(id+"F2.wireOp",EDGE,"E106.MirrorCS"),sQuery(id+"F2.wireOp",EDGE,"E107.MirrorCS"),sQuery(id+"F2.wireOp",EDGE,"E108.MirrorCS"),sQuery(id+"F2.wireOp",EDGE,"E109.MirrorCS"),sQuery(id+"F2.wireOp",EDGE,"E110.MirrorCS"),sQuery(id+"F2.wireOp",EDGE,"E111.MirrorCS"),sQuery(id+"F2.wireOp",EDGE,"E112.MirrorCS"),sQuery(id+"F2.wireOp",EDGE,"E113.MirrorCS"),sQuery(id+"F2.wireOp",EDGE,"E114.MirrorCS"),sQuery(id+"F2.wireOp",EDGE,"E115.MirrorCS"),sQuery(id+"F2.wireOp",EDGE,"E116.MirrorCS"),sQuery(id+"F2.wireOp",EDGE,"E117.MirrorCS"),sQuery(id+"F2.wireOp",EDGE,"E118.MirrorCS"),sQuery(id+"F2.wireOp",EDGE,"E121.MirrorCS"),sQuery(id+"F2.wireOp",EDGE,"E122.MirrorCS"),sQuery(id+"F2.wireOp",EDGE,"E123.bottom"),sQuery(id+"F2.wireOp",EDGE,"E123.left"),sQuery(id+"F2.wireOp",EDGE,"E138.bottom"),sQuery(id+"F2.wireOp",EDGE,"E138.left"),sQuery(id+"F2.wireOp",EDGE,"E153.bottom"),sQuery(id+"F2.wireOp",EDGE,"E153.left"),sQuery(id+"F2.wireOp",EDGE,"E169.bottom"),sQuery(id+"F2.wireOp",EDGE,"E169.left")])]});
            hole(context, id + "F17", {"style" : HoleStyle.SIMPLE, "endStyle" : HoleEndStyle.BLIND, "oppositeDirection" : true, "holeDiameter" : 9.4 * mm, "holeDepth" : 6 * mm, "isTappedThrough" : true, "tappedDepth" : 12 * mm, "tapClearance" : 3, "locations" : qUnion([Q0, Q1, Q2, Q3]), "scope" : qUnion([Q4])});
        }
        {
            var Q0;
            Q0=sQuery(id+"F16.wireOp",VERTEX,"E208");
            var Q1;
            Q1=sQuery(id+"F16.wireOp",VERTEX,"E209");
            var Q2;
            Q2=sQuery(id+"F16.wireOp",VERTEX,"E210.MirrorP");
            var Q3;
            Q3=sQuery(id+"F16.wireOp",VERTEX,"E211.MirrorP");
            var Q4;
            Q4=makeQuery(id+"F3.opExtrude","SWEPT_BODY",BODY,{"disambiguationData":[OSD([sQuery(id+"F2.wireOp",EDGE,"E19"),sQuery(id+"F2.wireOp",EDGE,"E25"),sQuery(id+"F2.wireOp",EDGE,"E12"),sQuery(id+"F2.wireOp",EDGE,"E10"),sQuery(id+"F2.wireOp",EDGE,"E24"),sQuery(id+"F2.wireOp",EDGE,"E17"),sQuery(id+"F2.wireOp",EDGE,"E15"),sQuery(id+"F2.wireOp",EDGE,"E16"),sQuery(id+"F2.wireOp",EDGE,"E11"),sQuery(id+"F2.wireOp",EDGE,"E18"),sQuery(id+"F2.wireOp",EDGE,"E13"),sQuery(id+"F2.wireOp",EDGE,"E26"),sQuery(id+"F2.wireOp",EDGE,"E9"),sQuery(id+"F2.wireOp",EDGE,"E27"),sQuery(id+"F2.wireOp",EDGE,"E21"),sQuery(id+"F2.wireOp",EDGE,"E14"),sQuery(id+"F2.wireOp",EDGE,"E20"),sQuery(id+"F2.wireOp",EDGE,"E23"),sQuery(id+"F2.wireOp",EDGE,"E8"),sQuery(id+"F2.wireOp",EDGE,"E22"),sQuery(id+"F2.wireOp",EDGE,"E47.bottom"),sQuery(id+"F2.wireOp",EDGE,"E47.top"),sQuery(id+"F2.wireOp",EDGE,"E47.left"),sQuery(id+"F2.wireOp",EDGE,"E47.right"),sQuery(id+"F2.wireOp",EDGE,"E48.MirrorCS"),sQuery(id+"F2.wireOp",EDGE,"E49.MirrorCS"),sQuery(id+"F2.wireOp",EDGE,"E50.MirrorCS"),sQuery(id+"F2.wireOp",EDGE,"E51.MirrorCS"),sQuery(id+"F2.wireOp",EDGE,"E52.MirrorCS"),sQuery(id+"F2.wireOp",EDGE,"E53.MirrorCS"),sQuery(id+"F2.wireOp",EDGE,"E54.MirrorCS"),sQuery(id+"F2.wireOp",EDGE,"E55.MirrorCS"),sQuery(id+"F2.wireOp",EDGE,"E58.MirrorCS"),sQuery(id+"F2.wireOp",EDGE,"E59.MirrorCS"),sQuery(id+"F2.wireOp",EDGE,"E60.MirrorCS"),sQuery(id+"F2.wireOp",EDGE,"E61.MirrorCS"),sQuery(id+"F2.wireOp",EDGE,"E62.MirrorCS"),sQuery(id+"F2.wireOp",EDGE,"E63.MirrorCS"),sQuery(id+"F2.wireOp",EDGE,"E64.MirrorCS"),sQuery(id+"F2.wireOp",EDGE,"E57.MirrorCS"),sQuery(id+"F2.wireOp",EDGE,"E65.MirrorCS"),sQuery(id+"F2.wireOp",EDGE,"E67.MirrorCS"),sQuery(id+"F2.wireOp",EDGE,"E68.MirrorCS"),sQuery(id+"F2.wireOp",EDGE,"E70.MirrorCS"),sQuery(id+"F2.wireOp",EDGE,"E71.MirrorCS"),sQuery(id+"F2.wireOp",EDGE,"E72.MirrorCS"),sQuery(id+"F2.wireOp",EDGE,"E73.MirrorCS"),sQuery(id+"F2.wireOp",EDGE,"E74.MirrorCS"),sQuery(id+"F2.wireOp",EDGE,"E75.MirrorCS"),sQuery(id+"F2.wireOp",EDGE,"E76.MirrorCS"),sQuery(id+"F2.wireOp",EDGE,"E77.MirrorCS"),sQuery(id+"F2.wireOp",EDGE,"E79.MirrorCS"),sQuery(id+"F2.wireOp",EDGE,"E92.MirrorCS"),sQuery(id+"F2.wireOp",EDGE,"E96.MirrorCS"),sQuery(id+"F2.wireOp",EDGE,"E97.MirrorCS"),sQuery(id+"F2.wireOp",EDGE,"E98.MirrorCS"),sQuery(id+"F2.wireOp",EDGE,"E99.MirrorCS"),sQuery(id+"F2.wireOp",EDGE,"E100.MirrorCS"),sQuery(id+"F2.wireOp",EDGE,"E101.MirrorCS"),sQuery(id+"F2.wireOp",EDGE,"E102.MirrorCS"),sQuery(id+"F2.wireOp",EDGE,"E87.MirrorCS"),sQuery(id+"F2.wireOp",EDGE,"E103.MirrorCS"),sQuery(id+"F2.wireOp",EDGE,"E83.MirrorCS"),sQuery(id+"F2.wireOp",EDGE,"E104.MirrorCS"),sQuery(id+"F2.wireOp",EDGE,"E105.MirrorCS"),sQuery(id+"F2.wireOp",EDGE,"E106.MirrorCS"),sQuery(id+"F2.wireOp",EDGE,"E107.MirrorCS"),sQuery(id+"F2.wireOp",EDGE,"E108.MirrorCS"),sQuery(id+"F2.wireOp",EDGE,"E109.MirrorCS"),sQuery(id+"F2.wireOp",EDGE,"E110.MirrorCS"),sQuery(id+"F2.wireOp",EDGE,"E111.MirrorCS"),sQuery(id+"F2.wireOp",EDGE,"E112.MirrorCS"),sQuery(id+"F2.wireOp",EDGE,"E113.MirrorCS"),sQuery(id+"F2.wireOp",EDGE,"E114.MirrorCS"),sQuery(id+"F2.wireOp",EDGE,"E115.MirrorCS"),sQuery(id+"F2.wireOp",EDGE,"E116.MirrorCS"),sQuery(id+"F2.wireOp",EDGE,"E117.MirrorCS"),sQuery(id+"F2.wireOp",EDGE,"E118.MirrorCS"),sQuery(id+"F2.wireOp",EDGE,"E121.MirrorCS"),sQuery(id+"F2.wireOp",EDGE,"E122.MirrorCS"),sQuery(id+"F2.wireOp",EDGE,"E123.bottom"),sQuery(id+"F2.wireOp",EDGE,"E123.left"),sQuery(id+"F2.wireOp",EDGE,"E138.bottom"),sQuery(id+"F2.wireOp",EDGE,"E138.left"),sQuery(id+"F2.wireOp",EDGE,"E153.bottom"),sQuery(id+"F2.wireOp",EDGE,"E153.left"),sQuery(id+"F2.wireOp",EDGE,"E169.bottom"),sQuery(id+"F2.wireOp",EDGE,"E169.left")])]});
            hole(context, id + "F18", {"style" : HoleStyle.SIMPLE, "endStyle" : HoleEndStyle.BLIND, "oppositeDirection" : true, "holeDiameter" : 12.4 * mm, "holeDepth" : 4 * mm, "isTappedThrough" : true, "tappedDepth" : 12 * mm, "tapClearance" : 3, "locations" : qUnion([Q0, Q1, Q2, Q3]), "scope" : qUnion([Q4])});
        }
        {
            var Q0;
            Q0=sQuery(id+"F16.wireOp",VERTEX,"E208");
            var Q1;
            Q1=sQuery(id+"F16.wireOp",VERTEX,"E209");
            var Q2;
            Q2=sQuery(id+"F16.wireOp",VERTEX,"E210.MirrorP");
            var Q3;
            Q3=sQuery(id+"F16.wireOp",VERTEX,"E211.MirrorP");
            var Q4;
            Q4=makeQuery(id+"F1.opExtrude","SWEPT_BODY",BODY,{"disambiguationData":[OSD([sQuery(id+"F0.wireOp",EDGE,"E3"),sQuery(id+"F0.wireOp",EDGE,"E4"),sQuery(id+"F0.wireOp",EDGE,"E2"),sQuery(id+"F0.wireOp",EDGE,"E5"),sQuery(id+"F0.wireOp",EDGE,"E0"),sQuery(id+"F0.wireOp",EDGE,"E1"),sQuery(id+"F0.wireOp",EDGE,"E6"),sQuery(id+"F0.wireOp",EDGE,"E7")])]});
            hole(context, id + "F19", {"style" : HoleStyle.SIMPLE, "endStyle" : HoleEndStyle.BLIND, "holeDiameter" : 9.4 * mm, "holeDepth" : 4 * mm, "isTappedThrough" : true, "tappedDepth" : 12 * mm, "tapClearance" : 3, "locations" : qUnion([Q0, Q1, Q2, Q3]), "scope" : qUnion([Q4])});
        }
        {
            var Q0;
            {var subQ4=sQuery(id+"F7.wireOp",EDGE,"E187.left");var subQ6=sQuery(id+"F7.wireOp",EDGE,"E185");var subQ7=makeQuery(id+"F7.imprint","INTERSECT",VERTEX,{"derivedFrom":[subQ6,subQ4]});Q0=makeQuery(id+"F7.imprint","IMPRINT",FACE,{"disambiguationData":[TD([[makeQuery(id+"F7.imprint","IMPRINT",EDGE,{"disambiguationData":[TD([[subQ7,1.0]])],"derivedFrom":subQ6}),1.0]])]});}
            extrude(context, id + "F20", {"entities" : qUnion([Q0]), "operationType" : NewBodyOperationType.REMOVE, "oppositeDirection" : true, "depth" : 25 * mm});
        }
        {
            var Q0;
            {var subQ4=sQuery(id+"F7.wireOp",EDGE,"E187.left");var subQ6=sQuery(id+"F7.wireOp",EDGE,"E185");var subQ7=makeQuery(id+"F7.imprint","INTERSECT",VERTEX,{"derivedFrom":[subQ6,subQ4]});Q0=makeQuery(id+"F7.imprint","IMPRINT",FACE,{"disambiguationData":[TD([[makeQuery(id+"F7.imprint","IMPRINT",EDGE,{"disambiguationData":[TD([[subQ7,1.0]])],"derivedFrom":subQ6}),1.0]])]});}
            var Q1;
            {var subQ0=sQuery(id+"F7.wireOp",EDGE,"E186");var subQ1=sQuery(id+"F7.wireOp",EDGE,"E185");var subQ2=makeQuery(id+"F7.imprint","INTERSECT",VERTEX,{"derivedFrom":[subQ1,subQ0]});Q1=makeQuery(id+"F7.imprint","IMPRINT",FACE,{"disambiguationData":[TD([[makeQuery(id+"F7.imprint","IMPRINT",EDGE,{"disambiguationData":[TD([[subQ2,1.0]])],"derivedFrom":subQ1}),1.0]])]});}
            var Q2;
            {var subQ0=sQuery(id+"F7.wireOp",EDGE,"E186");var subQ1=sQuery(id+"F7.wireOp",EDGE,"E185");var subQ2=makeQuery(id+"F7.imprint","INTERSECT",VERTEX,{"derivedFrom":[subQ1,subQ0]});Q2=makeQuery(id+"F7.imprint","IMPRINT",FACE,{"disambiguationData":[TD([[makeQuery(id+"F7.imprint","IMPRINT",EDGE,{"disambiguationData":[TD([[subQ2,-1.0]])],"derivedFrom":subQ1}),1.0]])]});}
            extrude(context, id + "F21", {"entities" : qUnion([Q0, Q1, Q2]), "operationType" : NewBodyOperationType.REMOVE, "depth" : 25 * mm});
        }
        {
            var Q0;
            Q0 = qSketchRegion(id + "F5", true);
            extrude(context, id + "F22", {"entities" : qUnion([Q0]), "operationType" : NewBodyOperationType.ADD, "oppositeDirection" : true, "depth" : 2 * mm, "offsetDistance" : 25 * mm});
        }
        {
            var Q0;
            Q0=makeQuery(id+"F6.boolean.opBoolean","INTERSECT",EDGE,{"derivedFrom":[makeQuery(id+"F1.opExtrude","CAP_FACE",FACE,{"disambiguationData":[OSD([sQuery(id+"F0.wireOp",EDGE,"E3"),sQuery(id+"F0.wireOp",EDGE,"E4"),sQuery(id+"F0.wireOp",EDGE,"E2"),sQuery(id+"F0.wireOp",EDGE,"E5"),sQuery(id+"F0.wireOp",EDGE,"E0"),sQuery(id+"F0.wireOp",EDGE,"E1"),sQuery(id+"F0.wireOp",EDGE,"E6"),sQuery(id+"F0.wireOp",EDGE,"E7")])],"isStart":false}),makeQuery(id+"F6.opExtrude","SWEPT_FACE",FACE,{"disambiguationData":[OSD([sQuery(id+"F5.wireOp",EDGE,"E181.MirrorC")])]})]});
            var Q1;
            Q1=makeQuery(id+"F6.boolean.opBoolean","INTERSECT",EDGE,{"derivedFrom":[makeQuery(id+"F1.opExtrude","CAP_FACE",FACE,{"disambiguationData":[OSD([sQuery(id+"F0.wireOp",EDGE,"E3"),sQuery(id+"F0.wireOp",EDGE,"E4"),sQuery(id+"F0.wireOp",EDGE,"E2"),sQuery(id+"F0.wireOp",EDGE,"E5"),sQuery(id+"F0.wireOp",EDGE,"E0"),sQuery(id+"F0.wireOp",EDGE,"E1"),sQuery(id+"F0.wireOp",EDGE,"E6"),sQuery(id+"F0.wireOp",EDGE,"E7")])],"isStart":false}),makeQuery(id+"F6.opExtrude","SWEPT_FACE",FACE,{"disambiguationData":[OSD([sQuery(id+"F5.wireOp",EDGE,"E183.MirrorC")])]})]});
            var Q2;
            Q2=makeQuery(id+"F6.boolean.opBoolean","INTERSECT",EDGE,{"derivedFrom":[makeQuery(id+"F1.opExtrude","CAP_FACE",FACE,{"disambiguationData":[OSD([sQuery(id+"F0.wireOp",EDGE,"E3"),sQuery(id+"F0.wireOp",EDGE,"E4"),sQuery(id+"F0.wireOp",EDGE,"E2"),sQuery(id+"F0.wireOp",EDGE,"E5"),sQuery(id+"F0.wireOp",EDGE,"E0"),sQuery(id+"F0.wireOp",EDGE,"E1"),sQuery(id+"F0.wireOp",EDGE,"E6"),sQuery(id+"F0.wireOp",EDGE,"E7")])],"isStart":false}),makeQuery(id+"F6.opExtrude","SWEPT_FACE",FACE,{"disambiguationData":[OSD([sQuery(id+"F5.wireOp",EDGE,"E180")])]})]});
            var Q3;
            Q3=makeQuery(id+"F6.boolean.opBoolean","INTERSECT",EDGE,{"derivedFrom":[makeQuery(id+"F1.opExtrude","CAP_FACE",FACE,{"disambiguationData":[OSD([sQuery(id+"F0.wireOp",EDGE,"E3"),sQuery(id+"F0.wireOp",EDGE,"E4"),sQuery(id+"F0.wireOp",EDGE,"E2"),sQuery(id+"F0.wireOp",EDGE,"E5"),sQuery(id+"F0.wireOp",EDGE,"E0"),sQuery(id+"F0.wireOp",EDGE,"E1"),sQuery(id+"F0.wireOp",EDGE,"E6"),sQuery(id+"F0.wireOp",EDGE,"E7")])],"isStart":false}),makeQuery(id+"F6.opExtrude","SWEPT_FACE",FACE,{"disambiguationData":[OSD([sQuery(id+"F5.wireOp",EDGE,"E182.MirrorC")])]})]});
            chamfer(context, id + "F23", {"entities" : qUnion([Q0, Q1, Q2, Q3]), "width" : 1.5 * mm, "tangentPropagation" : true});
        }
        {
            var Q0;
            Q0=makeQuery(id+"F22.boolean.opBoolean","MERGE",FACE,{"derivedFrom":[makeQuery(id+"F3.opExtrude","CAP_FACE",FACE,{"disambiguationData":[OSD([sQuery(id+"F2.wireOp",EDGE,"E19"),sQuery(id+"F2.wireOp",EDGE,"E25"),sQuery(id+"F2.wireOp",EDGE,"E12"),sQuery(id+"F2.wireOp",EDGE,"E10"),sQuery(id+"F2.wireOp",EDGE,"E24"),sQuery(id+"F2.wireOp",EDGE,"E17"),sQuery(id+"F2.wireOp",EDGE,"E15"),sQuery(id+"F2.wireOp",EDGE,"E16"),sQuery(id+"F2.wireOp",EDGE,"E11"),sQuery(id+"F2.wireOp",EDGE,"E18"),sQuery(id+"F2.wireOp",EDGE,"E13"),sQuery(id+"F2.wireOp",EDGE,"E26"),sQuery(id+"F2.wireOp",EDGE,"E9"),sQuery(id+"F2.wireOp",EDGE,"E27"),sQuery(id+"F2.wireOp",EDGE,"E21"),sQuery(id+"F2.wireOp",EDGE,"E14"),sQuery(id+"F2.wireOp",EDGE,"E20"),sQuery(id+"F2.wireOp",EDGE,"E23"),sQuery(id+"F2.wireOp",EDGE,"E8"),sQuery(id+"F2.wireOp",EDGE,"E22"),sQuery(id+"F2.wireOp",EDGE,"E47.bottom"),sQuery(id+"F2.wireOp",EDGE,"E47.top"),sQuery(id+"F2.wireOp",EDGE,"E47.left"),sQuery(id+"F2.wireOp",EDGE,"E47.right"),sQuery(id+"F2.wireOp",EDGE,"E48.MirrorCS"),sQuery(id+"F2.wireOp",EDGE,"E49.MirrorCS"),sQuery(id+"F2.wireOp",EDGE,"E50.MirrorCS"),sQuery(id+"F2.wireOp",EDGE,"E51.MirrorCS"),sQuery(id+"F2.wireOp",EDGE,"E52.MirrorCS"),sQuery(id+"F2.wireOp",EDGE,"E53.MirrorCS"),sQuery(id+"F2.wireOp",EDGE,"E54.MirrorCS"),sQuery(id+"F2.wireOp",EDGE,"E55.MirrorCS"),sQuery(id+"F2.wireOp",EDGE,"E58.MirrorCS"),sQuery(id+"F2.wireOp",EDGE,"E59.MirrorCS"),sQuery(id+"F2.wireOp",EDGE,"E60.MirrorCS"),sQuery(id+"F2.wireOp",EDGE,"E61.MirrorCS"),sQuery(id+"F2.wireOp",EDGE,"E62.MirrorCS"),sQuery(id+"F2.wireOp",EDGE,"E63.MirrorCS"),sQuery(id+"F2.wireOp",EDGE,"E64.MirrorCS"),sQuery(id+"F2.wireOp",EDGE,"E57.MirrorCS"),sQuery(id+"F2.wireOp",EDGE,"E65.MirrorCS"),sQuery(id+"F2.wireOp",EDGE,"E67.MirrorCS"),sQuery(id+"F2.wireOp",EDGE,"E68.MirrorCS"),sQuery(id+"F2.wireOp",EDGE,"E70.MirrorCS"),sQuery(id+"F2.wireOp",EDGE,"E71.MirrorCS"),sQuery(id+"F2.wireOp",EDGE,"E72.MirrorCS"),sQuery(id+"F2.wireOp",EDGE,"E73.MirrorCS"),sQuery(id+"F2.wireOp",EDGE,"E74.MirrorCS"),sQuery(id+"F2.wireOp",EDGE,"E75.MirrorCS"),sQuery(id+"F2.wireOp",EDGE,"E76.MirrorCS"),sQuery(id+"F2.wireOp",EDGE,"E77.MirrorCS"),sQuery(id+"F2.wireOp",EDGE,"E79.MirrorCS"),sQuery(id+"F2.wireOp",EDGE,"E92.MirrorCS"),sQuery(id+"F2.wireOp",EDGE,"E96.MirrorCS"),sQuery(id+"F2.wireOp",EDGE,"E97.MirrorCS"),sQuery(id+"F2.wireOp",EDGE,"E98.MirrorCS"),sQuery(id+"F2.wireOp",EDGE,"E99.MirrorCS"),sQuery(id+"F2.wireOp",EDGE,"E100.MirrorCS"),sQuery(id+"F2.wireOp",EDGE,"E101.MirrorCS"),sQuery(id+"F2.wireOp",EDGE,"E102.MirrorCS"),sQuery(id+"F2.wireOp",EDGE,"E87.MirrorCS"),sQuery(id+"F2.wireOp",EDGE,"E103.MirrorCS"),sQuery(id+"F2.wireOp",EDGE,"E83.MirrorCS"),sQuery(id+"F2.wireOp",EDGE,"E104.MirrorCS"),sQuery(id+"F2.wireOp",EDGE,"E105.MirrorCS"),sQuery(id+"F2.wireOp",EDGE,"E106.MirrorCS"),sQuery(id+"F2.wireOp",EDGE,"E107.MirrorCS"),sQuery(id+"F2.wireOp",EDGE,"E108.MirrorCS"),sQuery(id+"F2.wireOp",EDGE,"E109.MirrorCS"),sQuery(id+"F2.wireOp",EDGE,"E110.MirrorCS"),sQuery(id+"F2.wireOp",EDGE,"E111.MirrorCS"),sQuery(id+"F2.wireOp",EDGE,"E112.MirrorCS"),sQuery(id+"F2.wireOp",EDGE,"E113.MirrorCS"),sQuery(id+"F2.wireOp",EDGE,"E114.MirrorCS"),sQuery(id+"F2.wireOp",EDGE,"E115.MirrorCS"),sQuery(id+"F2.wireOp",EDGE,"E116.MirrorCS"),sQuery(id+"F2.wireOp",EDGE,"E117.MirrorCS"),sQuery(id+"F2.wireOp",EDGE,"E118.MirrorCS"),sQuery(id+"F2.wireOp",EDGE,"E121.MirrorCS"),sQuery(id+"F2.wireOp",EDGE,"E122.MirrorCS"),sQuery(id+"F2.wireOp",EDGE,"E123.bottom"),sQuery(id+"F2.wireOp",EDGE,"E123.left"),sQuery(id+"F2.wireOp",EDGE,"E138.bottom"),sQuery(id+"F2.wireOp",EDGE,"E138.left"),sQuery(id+"F2.wireOp",EDGE,"E153.bottom"),sQuery(id+"F2.wireOp",EDGE,"E153.left"),sQuery(id+"F2.wireOp",EDGE,"E169.bottom"),sQuery(id+"F2.wireOp",EDGE,"E169.left")])],"isStart":false}),makeQuery(id+"F22.opExtrude","CAP_FACE",FACE,{"disambiguationData":[OSD([sQuery(id+"F5.wireOp",EDGE,"E180")])],"isStart":true}),makeQuery(id+"F22.opExtrude","CAP_FACE",FACE,{"disambiguationData":[OSD([sQuery(id+"F5.wireOp",EDGE,"E181.MirrorC")])],"isStart":true}),makeQuery(id+"F22.opExtrude","CAP_FACE",FACE,{"disambiguationData":[OSD([sQuery(id+"F5.wireOp",EDGE,"E182.MirrorC")])],"isStart":true}),makeQuery(id+"F22.opExtrude","CAP_FACE",FACE,{"disambiguationData":[OSD([sQuery(id+"F5.wireOp",EDGE,"E183.MirrorC")])],"isStart":true})]});
            var sketch = newSketch(context, id + "F24", { "sketchPlane" : qUnion([Q0])});
            skLineSegment(sketch, "E212.bottom", {"start": v(-59.31, 28.79) * mm, "end": v(-46.71, 28.79) * mm});
            skLineSegment(sketch, "E212.top", {"start": v(-59.31, 16.19) * mm, "end": v(-46.71, 16.19) * mm});
            skLineSegment(sketch, "E212.left", {"start": v(-59.31, 28.79) * mm, "end": v(-59.31, 16.19) * mm});
            skLineSegment(sketch, "E212.right", {"start": v(-46.71, 28.79) * mm, "end": v(-46.71, 16.19) * mm});
            skPoint(sketch, "E212.middle", {"position": v(-53.01, 22.49) * mm});
            skPoint(sketch, "E212.middle.positionSnap0", {"position": v(-59.26, 22.49) * mm});
            skPoint(sketch, "E212.middle.positionSnap1", {"position": v(-53.01, 28.74) * mm});
            skPoint(sketch, "E212.centerSnap0", {"position": v(-59.26, 22.49) * mm});
            skPoint(sketch, "E212.centerSnap1", {"position": v(-53.01, 28.74) * mm});
            skPoint(sketch, "E213.0.1.0", {"position": v(-53.01, 7.5) * mm});
            skLineSegment(sketch, "E213.0.1.1", {"start": v(-59.31, 1.2) * mm, "end": v(-46.71, 1.2) * mm});
            skLineSegment(sketch, "E213.0.1.2", {"start": v(-59.31, 13.8) * mm, "end": v(-46.71, 13.8) * mm});
            skPoint(sketch, "E213.0.1.3", {"position": v(-59.26, 7.5) * mm});
            skLineSegment(sketch, "E213.0.1.4", {"start": v(-46.71, 13.8) * mm, "end": v(-46.71, 1.2) * mm});
            skPoint(sketch, "E213.0.1.5", {"position": v(-53.01, 13.75) * mm});
            skLineSegment(sketch, "E213.0.1.6", {"start": v(-59.31, 13.8) * mm, "end": v(-59.31, 1.2) * mm});
            skPoint(sketch, "E213.0.1.7", {"position": v(-53.01, 13.75) * mm});
            skPoint(sketch, "E213.0.1.8", {"position": v(-59.26, 7.5) * mm});
            skPoint(sketch, "E213.0.2.0", {"position": v(-53.01, -7.5) * mm});
            skLineSegment(sketch, "E213.0.2.1", {"start": v(-59.31, -13.8) * mm, "end": v(-46.71, -13.8) * mm});
            skLineSegment(sketch, "E213.0.2.2", {"start": v(-59.31, -1.2) * mm, "end": v(-46.71, -1.2) * mm});
            skPoint(sketch, "E213.0.2.3", {"position": v(-59.26, -7.5) * mm});
            skLineSegment(sketch, "E213.0.2.4", {"start": v(-46.71, -1.2) * mm, "end": v(-46.71, -13.8) * mm});
            skPoint(sketch, "E213.0.2.5", {"position": v(-53.01, -1.24) * mm});
            skLineSegment(sketch, "E213.0.2.6", {"start": v(-59.31, -1.2) * mm, "end": v(-59.31, -13.8) * mm});
            skPoint(sketch, "E213.0.2.7", {"position": v(-53.01, -1.24) * mm});
            skPoint(sketch, "E213.0.2.8", {"position": v(-59.26, -7.5) * mm});
            skPoint(sketch, "E213.0.3.0", {"position": v(-53.01, -22.48) * mm});
            skLineSegment(sketch, "E213.0.3.1", {"start": v(-59.31, -28.78) * mm, "end": v(-46.71, -28.78) * mm});
            skLineSegment(sketch, "E213.0.3.2", {"start": v(-59.31, -16.18) * mm, "end": v(-46.71, -16.18) * mm});
            skPoint(sketch, "E213.0.3.3", {"position": v(-59.26, -22.48) * mm});
            skLineSegment(sketch, "E213.0.3.4", {"start": v(-46.71, -16.18) * mm, "end": v(-46.71, -28.78) * mm});
            skPoint(sketch, "E213.0.3.5", {"position": v(-53.01, -16.23) * mm});
            skLineSegment(sketch, "E213.0.3.6", {"start": v(-59.31, -16.18) * mm, "end": v(-59.31, -28.78) * mm});
            skPoint(sketch, "E213.0.3.7", {"position": v(-53.01, -16.23) * mm});
            skPoint(sketch, "E213.0.3.8", {"position": v(-59.26, -22.48) * mm});
            skPoint(sketch, "E213.1.0.0", {"position": v(-38.02, 22.49) * mm});
            skLineSegment(sketch, "E213.1.0.1", {"start": v(-44.32, 16.19) * mm, "end": v(-31.72, 16.19) * mm});
            skLineSegment(sketch, "E213.1.0.2", {"start": v(-44.32, 28.79) * mm, "end": v(-31.72, 28.79) * mm});
            skPoint(sketch, "E213.1.0.3", {"position": v(-44.27, 22.49) * mm});
            skLineSegment(sketch, "E213.1.0.4", {"start": v(-31.72, 28.79) * mm, "end": v(-31.72, 16.19) * mm});
            skPoint(sketch, "E213.1.0.5", {"position": v(-38.02, 28.74) * mm});
            skLineSegment(sketch, "E213.1.0.6", {"start": v(-44.32, 28.79) * mm, "end": v(-44.32, 16.19) * mm});
            skPoint(sketch, "E213.1.0.7", {"position": v(-38.02, 28.74) * mm});
            skPoint(sketch, "E213.1.0.8", {"position": v(-44.27, 22.49) * mm});
            skPoint(sketch, "E213.1.1.0", {"position": v(-38.02, 7.5) * mm});
            skLineSegment(sketch, "E213.1.1.1", {"start": v(-44.32, 1.2) * mm, "end": v(-31.72, 1.2) * mm});
            skLineSegment(sketch, "E213.1.1.2", {"start": v(-44.32, 13.8) * mm, "end": v(-31.72, 13.8) * mm});
            skPoint(sketch, "E213.1.1.3", {"position": v(-44.27, 7.5) * mm});
            skLineSegment(sketch, "E213.1.1.4", {"start": v(-31.72, 13.8) * mm, "end": v(-31.72, 1.2) * mm});
            skPoint(sketch, "E213.1.1.5", {"position": v(-38.02, 13.75) * mm});
            skLineSegment(sketch, "E213.1.1.6", {"start": v(-44.32, 13.8) * mm, "end": v(-44.32, 1.2) * mm});
            skPoint(sketch, "E213.1.1.7", {"position": v(-38.02, 13.75) * mm});
            skPoint(sketch, "E213.1.1.8", {"position": v(-44.27, 7.5) * mm});
            skPoint(sketch, "E213.1.2.0", {"position": v(-38.02, -7.5) * mm});
            skLineSegment(sketch, "E213.1.2.1", {"start": v(-44.32, -13.8) * mm, "end": v(-31.72, -13.8) * mm});
            skLineSegment(sketch, "E213.1.2.2", {"start": v(-44.32, -1.2) * mm, "end": v(-31.72, -1.2) * mm});
            skPoint(sketch, "E213.1.2.3", {"position": v(-44.27, -7.5) * mm});
            skLineSegment(sketch, "E213.1.2.4", {"start": v(-31.72, -1.2) * mm, "end": v(-31.72, -13.8) * mm});
            skPoint(sketch, "E213.1.2.5", {"position": v(-38.02, -1.24) * mm});
            skLineSegment(sketch, "E213.1.2.6", {"start": v(-44.32, -1.2) * mm, "end": v(-44.32, -13.8) * mm});
            skPoint(sketch, "E213.1.2.7", {"position": v(-38.02, -1.24) * mm});
            skPoint(sketch, "E213.1.2.8", {"position": v(-44.27, -7.5) * mm});
            skPoint(sketch, "E213.1.3.0", {"position": v(-38.02, -22.48) * mm});
            skLineSegment(sketch, "E213.1.3.1", {"start": v(-44.32, -28.78) * mm, "end": v(-31.72, -28.78) * mm});
            skLineSegment(sketch, "E213.1.3.2", {"start": v(-44.32, -16.18) * mm, "end": v(-31.72, -16.18) * mm});
            skPoint(sketch, "E213.1.3.3", {"position": v(-44.27, -22.48) * mm});
            skLineSegment(sketch, "E213.1.3.4", {"start": v(-31.72, -16.18) * mm, "end": v(-31.72, -28.78) * mm});
            skPoint(sketch, "E213.1.3.5", {"position": v(-38.02, -16.23) * mm});
            skLineSegment(sketch, "E213.1.3.6", {"start": v(-44.32, -16.18) * mm, "end": v(-44.32, -28.78) * mm});
            skPoint(sketch, "E213.1.3.7", {"position": v(-38.02, -16.23) * mm});
            skPoint(sketch, "E213.1.3.8", {"position": v(-44.27, -22.48) * mm});
            skPoint(sketch, "E213.2.0.0", {"position": v(-23.03, 22.49) * mm});
            skLineSegment(sketch, "E213.2.0.1", {"start": v(-29.33, 16.19) * mm, "end": v(-16.73, 16.19) * mm});
            skLineSegment(sketch, "E213.2.0.2", {"start": v(-29.33, 28.79) * mm, "end": v(-16.73, 28.79) * mm});
            skPoint(sketch, "E213.2.0.3", {"position": v(-29.28, 22.49) * mm});
            skLineSegment(sketch, "E213.2.0.4", {"start": v(-16.73, 28.79) * mm, "end": v(-16.73, 16.19) * mm});
            skPoint(sketch, "E213.2.0.5", {"position": v(-23.03, 28.74) * mm});
            skLineSegment(sketch, "E213.2.0.6", {"start": v(-29.33, 28.79) * mm, "end": v(-29.33, 16.19) * mm});
            skPoint(sketch, "E213.2.0.7", {"position": v(-23.03, 28.74) * mm});
            skPoint(sketch, "E213.2.0.8", {"position": v(-29.28, 22.49) * mm});
            skPoint(sketch, "E213.2.1.0", {"position": v(-23.03, 7.5) * mm});
            skLineSegment(sketch, "E213.2.1.1", {"start": v(-29.33, 1.2) * mm, "end": v(-16.73, 1.2) * mm});
            skLineSegment(sketch, "E213.2.1.2", {"start": v(-29.33, 13.8) * mm, "end": v(-16.73, 13.8) * mm});
            skPoint(sketch, "E213.2.1.3", {"position": v(-29.28, 7.5) * mm});
            skLineSegment(sketch, "E213.2.1.4", {"start": v(-16.73, 13.8) * mm, "end": v(-16.73, 1.2) * mm});
            skPoint(sketch, "E213.2.1.5", {"position": v(-23.03, 13.75) * mm});
            skLineSegment(sketch, "E213.2.1.6", {"start": v(-29.33, 13.8) * mm, "end": v(-29.33, 1.2) * mm});
            skPoint(sketch, "E213.2.1.7", {"position": v(-23.03, 13.75) * mm});
            skPoint(sketch, "E213.2.1.8", {"position": v(-29.28, 7.5) * mm});
            skPoint(sketch, "E213.2.2.0", {"position": v(-23.03, -7.5) * mm});
            skLineSegment(sketch, "E213.2.2.1", {"start": v(-29.33, -13.8) * mm, "end": v(-16.73, -13.8) * mm});
            skLineSegment(sketch, "E213.2.2.2", {"start": v(-29.33, -1.2) * mm, "end": v(-16.73, -1.2) * mm});
            skPoint(sketch, "E213.2.2.3", {"position": v(-29.28, -7.5) * mm});
            skLineSegment(sketch, "E213.2.2.4", {"start": v(-16.73, -1.2) * mm, "end": v(-16.73, -13.8) * mm});
            skPoint(sketch, "E213.2.2.5", {"position": v(-23.03, -1.24) * mm});
            skLineSegment(sketch, "E213.2.2.6", {"start": v(-29.33, -1.2) * mm, "end": v(-29.33, -13.8) * mm});
            skPoint(sketch, "E213.2.2.7", {"position": v(-23.03, -1.24) * mm});
            skPoint(sketch, "E213.2.2.8", {"position": v(-29.28, -7.5) * mm});
            skPoint(sketch, "E213.2.3.0", {"position": v(-23.03, -22.48) * mm});
            skLineSegment(sketch, "E213.2.3.1", {"start": v(-29.33, -28.78) * mm, "end": v(-16.73, -28.78) * mm});
            skLineSegment(sketch, "E213.2.3.2", {"start": v(-29.33, -16.18) * mm, "end": v(-16.73, -16.18) * mm});
            skPoint(sketch, "E213.2.3.3", {"position": v(-29.28, -22.48) * mm});
            skLineSegment(sketch, "E213.2.3.4", {"start": v(-16.73, -16.18) * mm, "end": v(-16.73, -28.78) * mm});
            skPoint(sketch, "E213.2.3.5", {"position": v(-23.03, -16.23) * mm});
            skLineSegment(sketch, "E213.2.3.6", {"start": v(-29.33, -16.18) * mm, "end": v(-29.33, -28.78) * mm});
            skPoint(sketch, "E213.2.3.7", {"position": v(-23.03, -16.23) * mm});
            skPoint(sketch, "E213.2.3.8", {"position": v(-29.28, -22.48) * mm});
            skPoint(sketch, "E213.3.0.0", {"position": v(-8.04, 22.49) * mm});
            skLineSegment(sketch, "E213.3.0.1", {"start": v(-14.34, 16.19) * mm, "end": v(-1.74, 16.19) * mm});
            skLineSegment(sketch, "E213.3.0.2", {"start": v(-14.34, 28.79) * mm, "end": v(-1.74, 28.79) * mm});
            skPoint(sketch, "E213.3.0.3", {"position": v(-14.3, 22.49) * mm});
            skLineSegment(sketch, "E213.3.0.4", {"start": v(-1.74, 28.79) * mm, "end": v(-1.74, 16.19) * mm});
            skPoint(sketch, "E213.3.0.5", {"position": v(-8.04, 28.74) * mm});
            skLineSegment(sketch, "E213.3.0.6", {"start": v(-14.34, 28.79) * mm, "end": v(-14.34, 16.19) * mm});
            skPoint(sketch, "E213.3.0.7", {"position": v(-8.04, 28.74) * mm});
            skPoint(sketch, "E213.3.0.8", {"position": v(-14.3, 22.49) * mm});
            skPoint(sketch, "E213.3.1.0", {"position": v(-8.04, 7.5) * mm});
            skLineSegment(sketch, "E213.3.1.1", {"start": v(-14.34, 1.2) * mm, "end": v(-1.74, 1.2) * mm});
            skLineSegment(sketch, "E213.3.1.2", {"start": v(-14.34, 13.8) * mm, "end": v(-1.74, 13.8) * mm});
            skPoint(sketch, "E213.3.1.3", {"position": v(-14.3, 7.5) * mm});
            skLineSegment(sketch, "E213.3.1.4", {"start": v(-1.74, 13.8) * mm, "end": v(-1.74, 1.2) * mm});
            skPoint(sketch, "E213.3.1.5", {"position": v(-8.04, 13.75) * mm});
            skLineSegment(sketch, "E213.3.1.6", {"start": v(-14.34, 13.8) * mm, "end": v(-14.34, 1.2) * mm});
            skPoint(sketch, "E213.3.1.7", {"position": v(-8.04, 13.75) * mm});
            skPoint(sketch, "E213.3.1.8", {"position": v(-14.3, 7.5) * mm});
            skPoint(sketch, "E213.3.2.0", {"position": v(-8.04, -7.5) * mm});
            skLineSegment(sketch, "E213.3.2.1", {"start": v(-14.34, -13.8) * mm, "end": v(-1.74, -13.8) * mm});
            skLineSegment(sketch, "E213.3.2.2", {"start": v(-14.34, -1.2) * mm, "end": v(-1.74, -1.2) * mm});
            skPoint(sketch, "E213.3.2.3", {"position": v(-14.3, -7.5) * mm});
            skLineSegment(sketch, "E213.3.2.4", {"start": v(-1.74, -1.2) * mm, "end": v(-1.74, -13.8) * mm});
            skPoint(sketch, "E213.3.2.5", {"position": v(-8.04, -1.24) * mm});
            skLineSegment(sketch, "E213.3.2.6", {"start": v(-14.34, -1.2) * mm, "end": v(-14.34, -13.8) * mm});
            skPoint(sketch, "E213.3.2.7", {"position": v(-8.04, -1.24) * mm});
            skPoint(sketch, "E213.3.2.8", {"position": v(-14.3, -7.5) * mm});
            skLineSegment(sketch, "E213.direction1", {"start": v(-59.31, 16.19) * mm, "end": v(-44.32, 16.19) * mm, "construction": true});
            skLineSegment(sketch, "E213.direction2", {"start": v(-59.31, 16.19) * mm, "end": v(-59.31, 1.2) * mm, "construction": true});
            skSolve(sketch);
        }
        {
            var Q0;
            Q0 = qSketchRegion(id + "F24", true);
            extrude(context, id + "F25", {"entities" : qUnion([Q0]), "operationType" : NewBodyOperationType.REMOVE, "oppositeDirection" : true, "depth" : 25 * mm, "offsetDistance" : 25 * mm});
        }
        {
            var Q0;
            Q0=makeQuery(id+"F22.boolean.opBoolean","MERGE",FACE,{"derivedFrom":[makeQuery(id+"F3.opExtrude","CAP_FACE",FACE,{"disambiguationData":[OSD([sQuery(id+"F2.wireOp",EDGE,"E19"),sQuery(id+"F2.wireOp",EDGE,"E25"),sQuery(id+"F2.wireOp",EDGE,"E12"),sQuery(id+"F2.wireOp",EDGE,"E10"),sQuery(id+"F2.wireOp",EDGE,"E24"),sQuery(id+"F2.wireOp",EDGE,"E17"),sQuery(id+"F2.wireOp",EDGE,"E15"),sQuery(id+"F2.wireOp",EDGE,"E16"),sQuery(id+"F2.wireOp",EDGE,"E11"),sQuery(id+"F2.wireOp",EDGE,"E18"),sQuery(id+"F2.wireOp",EDGE,"E13"),sQuery(id+"F2.wireOp",EDGE,"E26"),sQuery(id+"F2.wireOp",EDGE,"E9"),sQuery(id+"F2.wireOp",EDGE,"E27"),sQuery(id+"F2.wireOp",EDGE,"E21"),sQuery(id+"F2.wireOp",EDGE,"E14"),sQuery(id+"F2.wireOp",EDGE,"E20"),sQuery(id+"F2.wireOp",EDGE,"E23"),sQuery(id+"F2.wireOp",EDGE,"E8"),sQuery(id+"F2.wireOp",EDGE,"E22"),sQuery(id+"F2.wireOp",EDGE,"E47.bottom"),sQuery(id+"F2.wireOp",EDGE,"E47.top"),sQuery(id+"F2.wireOp",EDGE,"E47.left"),sQuery(id+"F2.wireOp",EDGE,"E47.right"),sQuery(id+"F2.wireOp",EDGE,"E48.MirrorCS"),sQuery(id+"F2.wireOp",EDGE,"E49.MirrorCS"),sQuery(id+"F2.wireOp",EDGE,"E50.MirrorCS"),sQuery(id+"F2.wireOp",EDGE,"E51.MirrorCS"),sQuery(id+"F2.wireOp",EDGE,"E52.MirrorCS"),sQuery(id+"F2.wireOp",EDGE,"E53.MirrorCS"),sQuery(id+"F2.wireOp",EDGE,"E54.MirrorCS"),sQuery(id+"F2.wireOp",EDGE,"E55.MirrorCS"),sQuery(id+"F2.wireOp",EDGE,"E58.MirrorCS"),sQuery(id+"F2.wireOp",EDGE,"E59.MirrorCS"),sQuery(id+"F2.wireOp",EDGE,"E60.MirrorCS"),sQuery(id+"F2.wireOp",EDGE,"E61.MirrorCS"),sQuery(id+"F2.wireOp",EDGE,"E62.MirrorCS"),sQuery(id+"F2.wireOp",EDGE,"E63.MirrorCS"),sQuery(id+"F2.wireOp",EDGE,"E64.MirrorCS"),sQuery(id+"F2.wireOp",EDGE,"E57.MirrorCS"),sQuery(id+"F2.wireOp",EDGE,"E65.MirrorCS"),sQuery(id+"F2.wireOp",EDGE,"E67.MirrorCS"),sQuery(id+"F2.wireOp",EDGE,"E68.MirrorCS"),sQuery(id+"F2.wireOp",EDGE,"E70.MirrorCS"),sQuery(id+"F2.wireOp",EDGE,"E71.MirrorCS"),sQuery(id+"F2.wireOp",EDGE,"E72.MirrorCS"),sQuery(id+"F2.wireOp",EDGE,"E73.MirrorCS"),sQuery(id+"F2.wireOp",EDGE,"E74.MirrorCS"),sQuery(id+"F2.wireOp",EDGE,"E75.MirrorCS"),sQuery(id+"F2.wireOp",EDGE,"E76.MirrorCS"),sQuery(id+"F2.wireOp",EDGE,"E77.MirrorCS"),sQuery(id+"F2.wireOp",EDGE,"E79.MirrorCS"),sQuery(id+"F2.wireOp",EDGE,"E92.MirrorCS"),sQuery(id+"F2.wireOp",EDGE,"E96.MirrorCS"),sQuery(id+"F2.wireOp",EDGE,"E97.MirrorCS"),sQuery(id+"F2.wireOp",EDGE,"E98.MirrorCS"),sQuery(id+"F2.wireOp",EDGE,"E99.MirrorCS"),sQuery(id+"F2.wireOp",EDGE,"E100.MirrorCS"),sQuery(id+"F2.wireOp",EDGE,"E101.MirrorCS"),sQuery(id+"F2.wireOp",EDGE,"E102.MirrorCS"),sQuery(id+"F2.wireOp",EDGE,"E87.MirrorCS"),sQuery(id+"F2.wireOp",EDGE,"E103.MirrorCS"),sQuery(id+"F2.wireOp",EDGE,"E83.MirrorCS"),sQuery(id+"F2.wireOp",EDGE,"E104.MirrorCS"),sQuery(id+"F2.wireOp",EDGE,"E105.MirrorCS"),sQuery(id+"F2.wireOp",EDGE,"E106.MirrorCS"),sQuery(id+"F2.wireOp",EDGE,"E107.MirrorCS"),sQuery(id+"F2.wireOp",EDGE,"E108.MirrorCS"),sQuery(id+"F2.wireOp",EDGE,"E109.MirrorCS"),sQuery(id+"F2.wireOp",EDGE,"E110.MirrorCS"),sQuery(id+"F2.wireOp",EDGE,"E111.MirrorCS"),sQuery(id+"F2.wireOp",EDGE,"E112.MirrorCS"),sQuery(id+"F2.wireOp",EDGE,"E113.MirrorCS"),sQuery(id+"F2.wireOp",EDGE,"E114.MirrorCS"),sQuery(id+"F2.wireOp",EDGE,"E115.MirrorCS"),sQuery(id+"F2.wireOp",EDGE,"E116.MirrorCS"),sQuery(id+"F2.wireOp",EDGE,"E117.MirrorCS"),sQuery(id+"F2.wireOp",EDGE,"E118.MirrorCS"),sQuery(id+"F2.wireOp",EDGE,"E121.MirrorCS"),sQuery(id+"F2.wireOp",EDGE,"E122.MirrorCS"),sQuery(id+"F2.wireOp",EDGE,"E123.bottom"),sQuery(id+"F2.wireOp",EDGE,"E123.left"),sQuery(id+"F2.wireOp",EDGE,"E138.bottom"),sQuery(id+"F2.wireOp",EDGE,"E138.left"),sQuery(id+"F2.wireOp",EDGE,"E153.bottom"),sQuery(id+"F2.wireOp",EDGE,"E153.left"),sQuery(id+"F2.wireOp",EDGE,"E169.bottom"),sQuery(id+"F2.wireOp",EDGE,"E169.left")])],"isStart":false}),makeQuery(id+"F22.opExtrude","CAP_FACE",FACE,{"disambiguationData":[OSD([sQuery(id+"F5.wireOp",EDGE,"E180")])],"isStart":true}),makeQuery(id+"F22.opExtrude","CAP_FACE",FACE,{"disambiguationData":[OSD([sQuery(id+"F5.wireOp",EDGE,"E181.MirrorC")])],"isStart":true}),makeQuery(id+"F22.opExtrude","CAP_FACE",FACE,{"disambiguationData":[OSD([sQuery(id+"F5.wireOp",EDGE,"E182.MirrorC")])],"isStart":true}),makeQuery(id+"F22.opExtrude","CAP_FACE",FACE,{"disambiguationData":[OSD([sQuery(id+"F5.wireOp",EDGE,"E183.MirrorC")])],"isStart":true})]});
            var sketch = newSketch(context, id + "F26", { "sketchPlane" : qUnion([Q0])});
            skLineSegment(sketch, "E214.0", {"start": v(42.98, 27.7) * mm, "end": v(1.05, 27.7) * mm});
            skLineSegment(sketch, "E214.1", {"start": v(42.98, 17.27) * mm, "end": v(42.98, 27.7) * mm});
            skLineSegment(sketch, "E214.2", {"start": v(42.98, 17.27) * mm, "end": v(1.05, 17.27) * mm});
            skLineSegment(sketch, "E214.3", {"start": v(1.05, 17.27) * mm, "end": v(1.05, 27.7) * mm});
            skLineSegment(sketch, "E215.0", {"start": v(1.05, 12.71) * mm, "end": v(1.05, 2.28) * mm});
            skLineSegment(sketch, "E215.1", {"start": v(42.98, 12.71) * mm, "end": v(1.05, 12.71) * mm});
            skLineSegment(sketch, "E215.2", {"start": v(42.98, 12.71) * mm, "end": v(42.98, 2.28) * mm});
            skLineSegment(sketch, "E215.3", {"start": v(42.98, 2.28) * mm, "end": v(1.05, 2.28) * mm});
            skLineSegment(sketch, "E216.0", {"start": v(1.05, -12.71) * mm, "end": v(1.05, -2.28) * mm});
            skLineSegment(sketch, "E216.1", {"start": v(42.98, -12.71) * mm, "end": v(1.05, -12.71) * mm});
            skLineSegment(sketch, "E216.2", {"start": v(42.98, -12.71) * mm, "end": v(42.98, -2.28) * mm});
            skLineSegment(sketch, "E216.3", {"start": v(42.98, -2.28) * mm, "end": v(1.05, -2.28) * mm});
            skLineSegment(sketch, "E217.0", {"start": v(1.05, -17.27) * mm, "end": v(1.05, -27.7) * mm});
            skLineSegment(sketch, "E217.1", {"start": v(42.98, -17.27) * mm, "end": v(1.05, -17.27) * mm});
            skLineSegment(sketch, "E217.2", {"start": v(42.98, -17.27) * mm, "end": v(42.98, -27.7) * mm});
            skLineSegment(sketch, "E217.3", {"start": v(42.98, -27.7) * mm, "end": v(1.05, -27.7) * mm});
            skSolve(sketch);
        }
        {
            var Q0;
            Q0=makeQuery(id+"F26.imprint","IMPRINT",FACE,{"disambiguationData":[TD([[makeQuery(id+"F26.imprint","IMPRINT",EDGE,{"derivedFrom":sQuery(id+"F26.wireOp",EDGE,"E214.0")}),-1.0]])]});
            var Q1;
            Q1=makeQuery(id+"F26.imprint","IMPRINT",FACE,{"disambiguationData":[TD([[makeQuery(id+"F26.imprint","IMPRINT",EDGE,{"derivedFrom":sQuery(id+"F26.wireOp",EDGE,"E215.0")}),-1.0]])]});
            var Q2;
            Q2=makeQuery(id+"F26.imprint","IMPRINT",FACE,{"disambiguationData":[TD([[makeQuery(id+"F26.imprint","IMPRINT",EDGE,{"derivedFrom":sQuery(id+"F26.wireOp",EDGE,"E216.0")}),1.0]])]});
            var Q3;
            Q3=makeQuery(id+"F26.imprint","IMPRINT",FACE,{"disambiguationData":[TD([[makeQuery(id+"F26.imprint","IMPRINT",EDGE,{"derivedFrom":sQuery(id+"F26.wireOp",EDGE,"E217.0")}),-1.0]])]});
            extrude(context, id + "F27", {"entities" : qUnion([Q0, Q1, Q2, Q3]), "operationType" : NewBodyOperationType.ADD, "oppositeDirection" : true, "depth" : 0.5 * mm, "offsetDistance" : 25 * mm});
        }
        {
            var Q0;
            {var subQ0=sQuery(id+"F2.wireOp",EDGE,"E122.MirrorCS");var subQ1=sQuery(id+"F2.wireOp",EDGE,"E121.MirrorCS");var subQ2=sQuery(id+"F2.wireOp",EDGE,"E118.MirrorCS");var subQ3=sQuery(id+"F2.wireOp",EDGE,"E117.MirrorCS");var subQ4=sQuery(id+"F2.wireOp",EDGE,"E116.MirrorCS");var subQ5=sQuery(id+"F2.wireOp",EDGE,"E115.MirrorCS");var subQ6=sQuery(id+"F2.wireOp",EDGE,"E114.MirrorCS");var subQ7=sQuery(id+"F2.wireOp",EDGE,"E169.left");var subQ8=sQuery(id+"F2.wireOp",EDGE,"E113.MirrorCS");var subQ9=sQuery(id+"F2.wireOp",EDGE,"E112.MirrorCS");var subQ10=sQuery(id+"F2.wireOp",EDGE,"E169.bottom");var subQ11=sQuery(id+"F2.wireOp",EDGE,"E111.MirrorCS");var subQ12=sQuery(id+"F2.wireOp",EDGE,"E110.MirrorCS");var subQ13=sQuery(id+"F2.wireOp",EDGE,"E109.MirrorCS");var subQ14=sQuery(id+"F2.wireOp",EDGE,"E108.MirrorCS");var subQ15=sQuery(id+"F2.wireOp",EDGE,"E107.MirrorCS");var subQ16=sQuery(id+"F2.wireOp",EDGE,"E106.MirrorCS");var subQ17=sQuery(id+"F2.wireOp",EDGE,"E105.MirrorCS");var subQ18=sQuery(id+"F2.wireOp",EDGE,"E104.MirrorCS");var subQ19=sQuery(id+"F2.wireOp",EDGE,"E83.MirrorCS");var subQ20=sQuery(id+"F2.wireOp",EDGE,"E153.left");var subQ21=sQuery(id+"F2.wireOp",EDGE,"E103.MirrorCS");var subQ22=sQuery(id+"F2.wireOp",EDGE,"E87.MirrorCS");var subQ23=sQuery(id+"F2.wireOp",EDGE,"E102.MirrorCS");var subQ24=sQuery(id+"F2.wireOp",EDGE,"E101.MirrorCS");var subQ25=sQuery(id+"F2.wireOp",EDGE,"E100.MirrorCS");var subQ26=sQuery(id+"F2.wireOp",EDGE,"E99.MirrorCS");var subQ27=sQuery(id+"F2.wireOp",EDGE,"E98.MirrorCS");var subQ28=sQuery(id+"F2.wireOp",EDGE,"E97.MirrorCS");var subQ29=sQuery(id+"F2.wireOp",EDGE,"E96.MirrorCS");var subQ30=sQuery(id+"F2.wireOp",EDGE,"E153.bottom");var subQ31=sQuery(id+"F2.wireOp",EDGE,"E138.left");var subQ32=sQuery(id+"F2.wireOp",EDGE,"E138.bottom");var subQ33=sQuery(id+"F2.wireOp",EDGE,"E123.left");var subQ34=sQuery(id+"F2.wireOp",EDGE,"E123.bottom");var subQ35=sQuery(id+"F2.wireOp",EDGE,"E92.MirrorCS");var subQ36=sQuery(id+"F2.wireOp",EDGE,"E79.MirrorCS");var subQ37=sQuery(id+"F2.wireOp",EDGE,"E77.MirrorCS");var subQ38=sQuery(id+"F2.wireOp",EDGE,"E76.MirrorCS");var subQ39=sQuery(id+"F2.wireOp",EDGE,"E75.MirrorCS");var subQ40=sQuery(id+"F2.wireOp",EDGE,"E74.MirrorCS");var subQ41=sQuery(id+"F2.wireOp",EDGE,"E73.MirrorCS");var subQ42=sQuery(id+"F2.wireOp",EDGE,"E72.MirrorCS");var subQ43=sQuery(id+"F2.wireOp",EDGE,"E71.MirrorCS");var subQ44=sQuery(id+"F2.wireOp",EDGE,"E70.MirrorCS");var subQ45=sQuery(id+"F2.wireOp",EDGE,"E68.MirrorCS");var subQ46=sQuery(id+"F2.wireOp",EDGE,"E67.MirrorCS");var subQ47=sQuery(id+"F2.wireOp",EDGE,"E65.MirrorCS");var subQ48=sQuery(id+"F2.wireOp",EDGE,"E57.MirrorCS");var subQ49=sQuery(id+"F2.wireOp",EDGE,"E64.MirrorCS");var subQ50=sQuery(id+"F2.wireOp",EDGE,"E63.MirrorCS");var subQ51=sQuery(id+"F2.wireOp",EDGE,"E62.MirrorCS");var subQ52=sQuery(id+"F2.wireOp",EDGE,"E61.MirrorCS");var subQ53=sQuery(id+"F2.wireOp",EDGE,"E60.MirrorCS");var subQ54=sQuery(id+"F2.wireOp",EDGE,"E59.MirrorCS");var subQ55=sQuery(id+"F2.wireOp",EDGE,"E58.MirrorCS");var subQ56=sQuery(id+"F2.wireOp",EDGE,"E55.MirrorCS");var subQ57=sQuery(id+"F2.wireOp",EDGE,"E54.MirrorCS");var subQ58=sQuery(id+"F2.wireOp",EDGE,"E53.MirrorCS");var subQ59=sQuery(id+"F2.wireOp",EDGE,"E52.MirrorCS");var subQ60=sQuery(id+"F2.wireOp",EDGE,"E51.MirrorCS");var subQ61=sQuery(id+"F2.wireOp",EDGE,"E50.MirrorCS");var subQ62=sQuery(id+"F2.wireOp",EDGE,"E49.MirrorCS");var subQ63=sQuery(id+"F2.wireOp",EDGE,"E48.MirrorCS");var subQ64=sQuery(id+"F2.wireOp",EDGE,"E47.right");var subQ65=sQuery(id+"F2.wireOp",EDGE,"E47.left");var subQ66=sQuery(id+"F2.wireOp",EDGE,"E47.top");var subQ67=sQuery(id+"F2.wireOp",EDGE,"E47.bottom");var subQ68=sQuery(id+"F2.wireOp",EDGE,"E22");var subQ69=sQuery(id+"F2.wireOp",EDGE,"E8");var subQ70=sQuery(id+"F2.wireOp",EDGE,"E23");var subQ71=sQuery(id+"F2.wireOp",EDGE,"E20");var subQ72=sQuery(id+"F2.wireOp",EDGE,"E14");var subQ73=sQuery(id+"F2.wireOp",EDGE,"E21");var subQ74=sQuery(id+"F2.wireOp",EDGE,"E27");var subQ75=sQuery(id+"F2.wireOp",EDGE,"E9");var subQ76=sQuery(id+"F2.wireOp",EDGE,"E26");var subQ77=sQuery(id+"F2.wireOp",EDGE,"E13");var subQ78=sQuery(id+"F2.wireOp",EDGE,"E18");var subQ79=sQuery(id+"F2.wireOp",EDGE,"E11");var subQ80=sQuery(id+"F2.wireOp",EDGE,"E16");var subQ81=sQuery(id+"F2.wireOp",EDGE,"E15");var subQ82=sQuery(id+"F2.wireOp",EDGE,"E17");var subQ83=sQuery(id+"F2.wireOp",EDGE,"E24");var subQ84=sQuery(id+"F2.wireOp",EDGE,"E10");var subQ85=sQuery(id+"F2.wireOp",EDGE,"E12");var subQ86=sQuery(id+"F2.wireOp",EDGE,"E25");var subQ87=sQuery(id+"F2.wireOp",EDGE,"E19");var subQ88=makeQuery(id+"F3.opExtrude","CAP_FACE",FACE,{"disambiguationData":[OSD([subQ87,subQ86,subQ85,subQ84,subQ83,subQ82,subQ81,subQ80,subQ79,subQ78,subQ77,subQ76,subQ75,subQ74,subQ73,subQ72,subQ71,subQ70,subQ69,subQ68,subQ67,subQ66,subQ65,subQ64,subQ63,subQ62,subQ61,subQ60,subQ59,subQ58,subQ57,subQ56,subQ55,subQ54,subQ53,subQ52,subQ51,subQ50,subQ49,subQ48,subQ47,subQ46,subQ45,subQ44,subQ43,subQ42,subQ41,subQ40,subQ39,subQ38,subQ37,subQ36,subQ35,subQ29,subQ28,subQ27,subQ26,subQ25,subQ24,subQ23,subQ22,subQ21,subQ19,subQ18,subQ17,subQ16,subQ15,subQ14,subQ13,subQ12,subQ11,subQ9,subQ8,subQ6,subQ5,subQ4,subQ3,subQ2,subQ1,subQ0,subQ34,subQ33,subQ32,subQ31,subQ30,subQ20,subQ10,subQ7])],"isStart":true});Q0=makeQuery(id+"F8.boolean.opBoolean","SPLIT",FACE,{"disambiguationData":[TD([makeQuery(id+"F3.opExtrude","SWEPT_FACE",FACE,{"disambiguationData":[OSD([subQ87])]})])],"derivedFrom":subQ88});}
            var sketch = newSketch(context, id + "F28", { "sketchPlane" : qUnion([Q0])});
            skLineSegment(sketch, "E218.bottom", {"start": v(-43.51, 28.24) * mm, "end": v(-0.51, 28.24) * mm});
            skLineSegment(sketch, "E218.top", {"start": v(-43.51, 16.74) * mm, "end": v(-0.51, 16.74) * mm});
            skLineSegment(sketch, "E218.left", {"start": v(-43.51, 28.24) * mm, "end": v(-43.51, 16.74) * mm});
            skLineSegment(sketch, "E218.right", {"start": v(-0.51, 28.24) * mm, "end": v(-0.51, 16.74) * mm});
            skPoint(sketch, "E218.middle", {"position": v(-22.01, 22.49) * mm});
            skPoint(sketch, "E218.middle.positionSnap0", {"position": v(-43.48, 22.49) * mm});
            skPoint(sketch, "E218.middle.positionSnap1", {"position": v(-22.01, 28.2) * mm});
            skPoint(sketch, "E218.centerSnap0", {"position": v(-43.48, 22.49) * mm});
            skPoint(sketch, "E218.centerSnap1", {"position": v(-22.01, 28.2) * mm});
            skPoint(sketch, "E219.endSnap0", {"position": v(-43.48, 7.5) * mm});
            skLineSegment(sketch, "E220.0.1.0", {"start": v(-43.51, 13.25) * mm, "end": v(-0.51, 13.25) * mm});
            skPoint(sketch, "E220.0.1.1", {"position": v(-22.01, 7.5) * mm});
            skPoint(sketch, "E220.0.1.2", {"position": v(-22.01, 13.21) * mm});
            skLineSegment(sketch, "E220.0.1.3", {"start": v(-43.51, 1.75) * mm, "end": v(-0.51, 1.75) * mm});
            skLineSegment(sketch, "E220.0.1.4", {"start": v(-0.51, 13.25) * mm, "end": v(-0.51, 1.75) * mm});
            skLineSegment(sketch, "E220.0.1.6", {"start": v(-43.51, 13.25) * mm, "end": v(-43.51, 1.75) * mm});
            skPoint(sketch, "E220.0.1.7", {"position": v(-22.01, 13.21) * mm});
            skLineSegment(sketch, "E220.0.2.0", {"start": v(-43.51, -1.74) * mm, "end": v(-0.51, -1.74) * mm});
            skPoint(sketch, "E220.0.2.1", {"position": v(-22.01, -7.5) * mm});
            skPoint(sketch, "E220.0.2.2", {"position": v(-22.01, -1.78) * mm});
            skLineSegment(sketch, "E220.0.2.3", {"start": v(-43.51, -13.24) * mm, "end": v(-0.51, -13.24) * mm});
            skLineSegment(sketch, "E220.0.2.4", {"start": v(-0.51, -1.74) * mm, "end": v(-0.51, -13.24) * mm});
            skPoint(sketch, "E220.0.2.5", {"position": v(-43.48, -7.5) * mm});
            skLineSegment(sketch, "E220.0.2.6", {"start": v(-43.51, -1.74) * mm, "end": v(-43.51, -13.24) * mm});
            skPoint(sketch, "E220.0.2.7", {"position": v(-22.01, -1.78) * mm});
            skPoint(sketch, "E220.0.2.8", {"position": v(-43.48, -7.5) * mm});
            skLineSegment(sketch, "E220.0.3.0", {"start": v(-43.51, -16.73) * mm, "end": v(-0.51, -16.73) * mm});
            skPoint(sketch, "E220.0.3.1", {"position": v(-22.01, -22.48) * mm});
            skPoint(sketch, "E220.0.3.2", {"position": v(-22.01, -16.77) * mm});
            skLineSegment(sketch, "E220.0.3.3", {"start": v(-43.51, -28.23) * mm, "end": v(-0.51, -28.23) * mm});
            skLineSegment(sketch, "E220.0.3.4", {"start": v(-0.51, -16.73) * mm, "end": v(-0.51, -28.23) * mm});
            skPoint(sketch, "E220.0.3.5", {"position": v(-43.48, -22.48) * mm});
            skLineSegment(sketch, "E220.0.3.6", {"start": v(-43.51, -16.73) * mm, "end": v(-43.51, -28.23) * mm});
            skPoint(sketch, "E220.0.3.7", {"position": v(-22.01, -16.77) * mm});
            skPoint(sketch, "E220.0.3.8", {"position": v(-43.48, -22.48) * mm});
            skLineSegment(sketch, "E220.direction1", {"start": v(-43.51, 16.74) * mm, "end": v(-18.51, 16.74) * mm, "construction": true});
            skLineSegment(sketch, "E220.direction2", {"start": v(-43.51, 16.74) * mm, "end": v(-43.51, 1.75) * mm, "construction": true});
            skSolve(sketch);
        }
        {
            var Q0;
            Q0 = qSketchRegion(id + "F28", true);
            var Q1;
            Q1=makeQuery(id+"F27.opExtrude","CAP_FACE",FACE,{"disambiguationData":[OSD([sQuery(id+"F10.wireOp",EDGE,"E188.bottom"),sQuery(id+"F10.wireOp",EDGE,"E188.top"),sQuery(id+"F10.wireOp",EDGE,"E188.left"),sQuery(id+"F10.wireOp",EDGE,"E188.right"),sQuery(id+"F10.wireOp",EDGE,"E201.left"),sQuery(id+"F10.wireOp",EDGE,"E201.right"),sQuery(id+"F26.wireOp",EDGE,"E214.0"),sQuery(id+"F26.wireOp",EDGE,"E214.1"),sQuery(id+"F26.wireOp",EDGE,"E214.2"),sQuery(id+"F26.wireOp",EDGE,"E214.3")])],"isStart":false});
            extrude(context, id + "F29", {"entities" : qUnion([Q0]), "operationType" : NewBodyOperationType.REMOVE, "endBound" : BoundingType.UP_TO_SURFACE, "oppositeDirection" : true, "depth" : 5.5 * mm, "endBoundEntityFace" : qUnion([Q1]), "offsetDistance" : 25 * mm});
        }
        {
            var Q0;
            Q0=makeQuery(id+"F1.opExtrude","CAP_FACE",FACE,{"disambiguationData":[OSD([sQuery(id+"F0.wireOp",EDGE,"E3"),sQuery(id+"F0.wireOp",EDGE,"E4"),sQuery(id+"F0.wireOp",EDGE,"E2"),sQuery(id+"F0.wireOp",EDGE,"E5"),sQuery(id+"F0.wireOp",EDGE,"E0"),sQuery(id+"F0.wireOp",EDGE,"E1"),sQuery(id+"F0.wireOp",EDGE,"E6"),sQuery(id+"F0.wireOp",EDGE,"E7")])],"isStart":true});
            var sketch = newSketch(context, id + "F30", { "sketchPlane" : qUnion([Q0])});
            skLineSegment(sketch, "E221.bottom", {"start": v(-52.01, 27.74) * mm, "end": v(-54.01, 27.74) * mm});
            skLineSegment(sketch, "E221.left", {"start": v(-52.01, 27.74) * mm, "end": v(-52.01, 28.74) * mm});
            skLineSegment(sketch, "E221.right", {"start": v(-54.01, 27.74) * mm, "end": v(-54.01, 28.74) * mm});
            skPoint(sketch, "E221.middle", {"position": v(-53.01, 28.74) * mm});
            skLineSegment(sketch, "E222", {"start": v(-54.01, 28.74) * mm, "end": v(-52.01, 28.74) * mm});
            skLineSegment(sketch, "E223.0.1.0", {"start": v(-54.01, 12.75) * mm, "end": v(-54.01, 13.75) * mm});
            skLineSegment(sketch, "E223.0.1.1", {"start": v(-54.01, 13.75) * mm, "end": v(-52.01, 13.75) * mm});
            skLineSegment(sketch, "E223.0.1.2", {"start": v(-52.01, 12.75) * mm, "end": v(-52.01, 13.75) * mm});
            skLineSegment(sketch, "E223.0.2.0", {"start": v(-54.01, -2.24) * mm, "end": v(-54.01, -1.24) * mm});
            skLineSegment(sketch, "E223.0.2.1", {"start": v(-54.01, -1.24) * mm, "end": v(-52.01, -1.24) * mm});
            skLineSegment(sketch, "E223.0.2.2", {"start": v(-52.01, -2.24) * mm, "end": v(-52.01, -1.24) * mm});
            skLineSegment(sketch, "E223.0.3.0", {"start": v(-54.01, -17.23) * mm, "end": v(-54.01, -16.23) * mm});
            skLineSegment(sketch, "E223.0.3.1", {"start": v(-54.01, -16.23) * mm, "end": v(-52.01, -16.23) * mm});
            skLineSegment(sketch, "E223.0.3.2", {"start": v(-52.01, -17.23) * mm, "end": v(-52.01, -16.23) * mm});
            skLineSegment(sketch, "E223.1.0.0", {"start": v(-39.02, 27.74) * mm, "end": v(-39.02, 28.74) * mm});
            skLineSegment(sketch, "E223.1.0.1", {"start": v(-39.02, 28.74) * mm, "end": v(-37.02, 28.74) * mm});
            skLineSegment(sketch, "E223.1.0.2", {"start": v(-37.02, 27.74) * mm, "end": v(-37.02, 28.74) * mm});
            skLineSegment(sketch, "E223.1.1.0", {"start": v(-39.02, 12.75) * mm, "end": v(-39.02, 13.75) * mm});
            skLineSegment(sketch, "E223.1.1.1", {"start": v(-39.02, 13.75) * mm, "end": v(-37.02, 13.75) * mm});
            skLineSegment(sketch, "E223.1.1.2", {"start": v(-37.02, 12.75) * mm, "end": v(-37.02, 13.75) * mm});
            skLineSegment(sketch, "E223.1.2.0", {"start": v(-39.02, -2.24) * mm, "end": v(-39.02, -1.24) * mm});
            skLineSegment(sketch, "E223.1.2.1", {"start": v(-39.02, -1.24) * mm, "end": v(-37.02, -1.24) * mm});
            skLineSegment(sketch, "E223.1.2.2", {"start": v(-37.02, -2.24) * mm, "end": v(-37.02, -1.24) * mm});
            skLineSegment(sketch, "E223.1.3.0", {"start": v(-39.02, -17.23) * mm, "end": v(-39.02, -16.23) * mm});
            skLineSegment(sketch, "E223.1.3.1", {"start": v(-39.02, -16.23) * mm, "end": v(-37.02, -16.23) * mm});
            skLineSegment(sketch, "E223.1.3.2", {"start": v(-37.02, -17.23) * mm, "end": v(-37.02, -16.23) * mm});
            skLineSegment(sketch, "E223.2.0.0", {"start": v(-24.03, 27.74) * mm, "end": v(-24.03, 28.74) * mm});
            skLineSegment(sketch, "E223.2.0.1", {"start": v(-24.03, 28.74) * mm, "end": v(-22.03, 28.74) * mm});
            skLineSegment(sketch, "E223.2.0.2", {"start": v(-22.03, 27.74) * mm, "end": v(-22.03, 28.74) * mm});
            skLineSegment(sketch, "E223.2.1.0", {"start": v(-24.03, 12.75) * mm, "end": v(-24.03, 13.75) * mm});
            skLineSegment(sketch, "E223.2.1.1", {"start": v(-24.03, 13.75) * mm, "end": v(-22.03, 13.75) * mm});
            skLineSegment(sketch, "E223.2.1.2", {"start": v(-22.03, 12.75) * mm, "end": v(-22.03, 13.75) * mm});
            skLineSegment(sketch, "E223.2.2.0", {"start": v(-24.03, -2.24) * mm, "end": v(-24.03, -1.24) * mm});
            skLineSegment(sketch, "E223.2.2.1", {"start": v(-24.03, -1.24) * mm, "end": v(-22.03, -1.24) * mm});
            skLineSegment(sketch, "E223.2.2.2", {"start": v(-22.03, -2.24) * mm, "end": v(-22.03, -1.24) * mm});
            skLineSegment(sketch, "E223.2.3.0", {"start": v(-24.03, -17.23) * mm, "end": v(-24.03, -16.23) * mm});
            skLineSegment(sketch, "E223.2.3.1", {"start": v(-24.03, -16.23) * mm, "end": v(-22.03, -16.23) * mm});
            skLineSegment(sketch, "E223.2.3.2", {"start": v(-22.03, -17.23) * mm, "end": v(-22.03, -16.23) * mm});
            skLineSegment(sketch, "E223.3.0.0", {"start": v(-9.04, 27.74) * mm, "end": v(-9.04, 28.74) * mm});
            skLineSegment(sketch, "E223.3.0.1", {"start": v(-9.04, 28.74) * mm, "end": v(-7.04, 28.74) * mm});
            skLineSegment(sketch, "E223.3.0.2", {"start": v(-7.04, 27.74) * mm, "end": v(-7.04, 28.74) * mm});
            skLineSegment(sketch, "E223.3.1.0", {"start": v(-9.04, 12.75) * mm, "end": v(-9.04, 13.75) * mm});
            skLineSegment(sketch, "E223.3.1.1", {"start": v(-9.04, 13.75) * mm, "end": v(-7.04, 13.75) * mm});
            skLineSegment(sketch, "E223.3.1.2", {"start": v(-7.04, 12.75) * mm, "end": v(-7.04, 13.75) * mm});
            skLineSegment(sketch, "E223.3.2.0", {"start": v(-9.04, -2.24) * mm, "end": v(-9.04, -1.24) * mm});
            skLineSegment(sketch, "E223.3.2.1", {"start": v(-9.04, -1.24) * mm, "end": v(-7.04, -1.24) * mm});
            skLineSegment(sketch, "E223.3.2.2", {"start": v(-7.04, -2.24) * mm, "end": v(-7.04, -1.24) * mm});
            skLineSegment(sketch, "E224", {"start": v(-39.02, 27.74) * mm, "end": v(-37.02, 27.74) * mm});
            skLineSegment(sketch, "E225", {"start": v(-24.03, 27.74) * mm, "end": v(-22.03, 27.74) * mm});
            skLineSegment(sketch, "E226", {"start": v(-9.04, 27.74) * mm, "end": v(-7.04, 27.74) * mm});
            skLineSegment(sketch, "E227", {"start": v(-9.04, 12.75) * mm, "end": v(-7.04, 12.75) * mm});
            skLineSegment(sketch, "E228", {"start": v(-24.03, 12.75) * mm, "end": v(-22.03, 12.75) * mm});
            skLineSegment(sketch, "E229", {"start": v(-39.02, 12.75) * mm, "end": v(-37.02, 12.75) * mm});
            skLineSegment(sketch, "E230", {"start": v(-54.01, 12.75) * mm, "end": v(-52.01, 12.75) * mm});
            skLineSegment(sketch, "E231", {"start": v(-54.01, -2.24) * mm, "end": v(-52.01, -2.24) * mm});
            skLineSegment(sketch, "E232", {"start": v(-39.02, -2.24) * mm, "end": v(-37.02, -2.24) * mm});
            skLineSegment(sketch, "E233", {"start": v(-24.03, -2.24) * mm, "end": v(-22.03, -2.24) * mm});
            skLineSegment(sketch, "E234", {"start": v(-9.04, -2.24) * mm, "end": v(-7.04, -2.24) * mm});
            skLineSegment(sketch, "E235", {"start": v(-54.01, -17.23) * mm, "end": v(-52.01, -17.23) * mm});
            skLineSegment(sketch, "E236", {"start": v(-39.02, -17.23) * mm, "end": v(-37.02, -17.23) * mm});
            skLineSegment(sketch, "E237", {"start": v(-24.03, -17.23) * mm, "end": v(-22.03, -17.23) * mm});
            skLineSegment(sketch, "E238.bottom", {"start": v(-52.01, 16.24) * mm, "end": v(-54.01, 16.24) * mm});
            skLineSegment(sketch, "E238.top", {"start": v(-52.01, 17.24) * mm, "end": v(-54.01, 17.24) * mm});
            skLineSegment(sketch, "E238.left", {"start": v(-52.01, 16.24) * mm, "end": v(-52.01, 17.24) * mm});
            skLineSegment(sketch, "E238.right", {"start": v(-54.01, 16.24) * mm, "end": v(-54.01, 17.24) * mm});
            skLineSegment(sketch, "E239.0.1.0", {"start": v(-52.01, 1.25) * mm, "end": v(-52.01, 2.25) * mm});
            skLineSegment(sketch, "E239.0.1.1", {"start": v(-52.01, 2.25) * mm, "end": v(-54.01, 2.25) * mm});
            skLineSegment(sketch, "E239.0.1.3", {"start": v(-52.01, 1.25) * mm, "end": v(-54.01, 1.25) * mm});
            skLineSegment(sketch, "E239.0.1.4", {"start": v(-54.01, 1.25) * mm, "end": v(-54.01, 2.25) * mm});
            skLineSegment(sketch, "E239.0.2.0", {"start": v(-52.01, -13.75) * mm, "end": v(-52.01, -12.75) * mm});
            skLineSegment(sketch, "E239.0.2.1", {"start": v(-52.01, -12.75) * mm, "end": v(-54.01, -12.75) * mm});
            skLineSegment(sketch, "E239.0.2.3", {"start": v(-52.01, -13.75) * mm, "end": v(-54.01, -13.75) * mm});
            skLineSegment(sketch, "E239.0.2.4", {"start": v(-54.01, -13.75) * mm, "end": v(-54.01, -12.75) * mm});
            skLineSegment(sketch, "E239.0.3.0", {"start": v(-52.01, -28.74) * mm, "end": v(-52.01, -27.74) * mm});
            skLineSegment(sketch, "E239.0.3.1", {"start": v(-52.01, -27.74) * mm, "end": v(-54.01, -27.74) * mm});
            skLineSegment(sketch, "E239.0.3.3", {"start": v(-52.01, -28.74) * mm, "end": v(-54.01, -28.74) * mm});
            skLineSegment(sketch, "E239.0.3.4", {"start": v(-54.01, -28.74) * mm, "end": v(-54.01, -27.74) * mm});
            skLineSegment(sketch, "E239.1.0.0", {"start": v(-37.02, 16.24) * mm, "end": v(-37.02, 17.24) * mm});
            skLineSegment(sketch, "E239.1.0.1", {"start": v(-37.02, 17.24) * mm, "end": v(-39.02, 17.24) * mm});
            skLineSegment(sketch, "E239.1.0.3", {"start": v(-37.02, 16.24) * mm, "end": v(-39.02, 16.24) * mm});
            skLineSegment(sketch, "E239.1.0.4", {"start": v(-39.02, 16.24) * mm, "end": v(-39.02, 17.24) * mm});
            skLineSegment(sketch, "E239.1.1.0", {"start": v(-37.02, 1.25) * mm, "end": v(-37.02, 2.25) * mm});
            skLineSegment(sketch, "E239.1.1.1", {"start": v(-37.02, 2.25) * mm, "end": v(-39.02, 2.25) * mm});
            skLineSegment(sketch, "E239.1.1.3", {"start": v(-37.02, 1.25) * mm, "end": v(-39.02, 1.25) * mm});
            skLineSegment(sketch, "E239.1.1.4", {"start": v(-39.02, 1.25) * mm, "end": v(-39.02, 2.25) * mm});
            skLineSegment(sketch, "E239.1.2.0", {"start": v(-37.02, -13.75) * mm, "end": v(-37.02, -12.75) * mm});
            skLineSegment(sketch, "E239.1.2.1", {"start": v(-37.02, -12.75) * mm, "end": v(-39.02, -12.75) * mm});
            skLineSegment(sketch, "E239.1.2.3", {"start": v(-37.02, -13.75) * mm, "end": v(-39.02, -13.75) * mm});
            skLineSegment(sketch, "E239.1.2.4", {"start": v(-39.02, -13.75) * mm, "end": v(-39.02, -12.75) * mm});
            skLineSegment(sketch, "E239.1.3.0", {"start": v(-37.02, -28.74) * mm, "end": v(-37.02, -27.74) * mm});
            skLineSegment(sketch, "E239.1.3.1", {"start": v(-37.02, -27.74) * mm, "end": v(-39.02, -27.74) * mm});
            skLineSegment(sketch, "E239.1.3.3", {"start": v(-37.02, -28.74) * mm, "end": v(-39.02, -28.74) * mm});
            skLineSegment(sketch, "E239.1.3.4", {"start": v(-39.02, -28.74) * mm, "end": v(-39.02, -27.74) * mm});
            skLineSegment(sketch, "E239.2.0.0", {"start": v(-22.03, 16.24) * mm, "end": v(-22.03, 17.24) * mm});
            skLineSegment(sketch, "E239.2.0.1", {"start": v(-22.03, 17.24) * mm, "end": v(-24.03, 17.24) * mm});
            skLineSegment(sketch, "E239.2.0.3", {"start": v(-22.03, 16.24) * mm, "end": v(-24.03, 16.24) * mm});
            skLineSegment(sketch, "E239.2.0.4", {"start": v(-24.03, 16.24) * mm, "end": v(-24.03, 17.24) * mm});
            skLineSegment(sketch, "E239.2.1.0", {"start": v(-22.03, 1.25) * mm, "end": v(-22.03, 2.25) * mm});
            skLineSegment(sketch, "E239.2.1.1", {"start": v(-22.03, 2.25) * mm, "end": v(-24.03, 2.25) * mm});
            skLineSegment(sketch, "E239.2.1.3", {"start": v(-22.03, 1.25) * mm, "end": v(-24.03, 1.25) * mm});
            skLineSegment(sketch, "E239.2.1.4", {"start": v(-24.03, 1.25) * mm, "end": v(-24.03, 2.25) * mm});
            skLineSegment(sketch, "E239.2.2.0", {"start": v(-22.03, -13.75) * mm, "end": v(-22.03, -12.75) * mm});
            skLineSegment(sketch, "E239.2.2.1", {"start": v(-22.03, -12.75) * mm, "end": v(-24.03, -12.75) * mm});
            skLineSegment(sketch, "E239.2.2.3", {"start": v(-22.03, -13.75) * mm, "end": v(-24.03, -13.75) * mm});
            skLineSegment(sketch, "E239.2.2.4", {"start": v(-24.03, -13.75) * mm, "end": v(-24.03, -12.75) * mm});
            skLineSegment(sketch, "E239.2.3.0", {"start": v(-22.03, -28.74) * mm, "end": v(-22.03, -27.74) * mm});
            skLineSegment(sketch, "E239.2.3.1", {"start": v(-22.03, -27.74) * mm, "end": v(-24.03, -27.74) * mm});
            skLineSegment(sketch, "E239.2.3.3", {"start": v(-22.03, -28.74) * mm, "end": v(-24.03, -28.74) * mm});
            skLineSegment(sketch, "E239.2.3.4", {"start": v(-24.03, -28.74) * mm, "end": v(-24.03, -27.74) * mm});
            skLineSegment(sketch, "E239.3.0.0", {"start": v(-7.04, 16.24) * mm, "end": v(-7.04, 17.24) * mm});
            skLineSegment(sketch, "E239.3.0.1", {"start": v(-7.04, 17.24) * mm, "end": v(-9.04, 17.24) * mm});
            skLineSegment(sketch, "E239.3.0.3", {"start": v(-7.04, 16.24) * mm, "end": v(-9.04, 16.24) * mm});
            skLineSegment(sketch, "E239.3.0.4", {"start": v(-9.04, 16.24) * mm, "end": v(-9.04, 17.24) * mm});
            skLineSegment(sketch, "E239.3.1.0", {"start": v(-7.04, 1.25) * mm, "end": v(-7.04, 2.25) * mm});
            skLineSegment(sketch, "E239.3.1.1", {"start": v(-7.04, 2.25) * mm, "end": v(-9.04, 2.25) * mm});
            skLineSegment(sketch, "E239.3.1.3", {"start": v(-7.04, 1.25) * mm, "end": v(-9.04, 1.25) * mm});
            skLineSegment(sketch, "E239.3.1.4", {"start": v(-9.04, 1.25) * mm, "end": v(-9.04, 2.25) * mm});
            skLineSegment(sketch, "E239.3.2.0", {"start": v(-7.04, -13.75) * mm, "end": v(-7.04, -12.75) * mm});
            skLineSegment(sketch, "E239.3.2.1", {"start": v(-7.04, -12.75) * mm, "end": v(-9.04, -12.75) * mm});
            skLineSegment(sketch, "E239.3.2.3", {"start": v(-7.04, -13.75) * mm, "end": v(-9.04, -13.75) * mm});
            skLineSegment(sketch, "E239.3.2.4", {"start": v(-9.04, -13.75) * mm, "end": v(-9.04, -12.75) * mm});
            skSolve(sketch);
        }
        {
            var Q0;
            Q0 = qSketchRegion(id + "F30", true);
            extrude(context, id + "F31", {"entities" : qUnion([Q0]), "operationType" : NewBodyOperationType.ADD, "oppositeDirection" : true, "depth" : 3 * mm, "offsetDistance" : 25 * mm});
        }
    });
